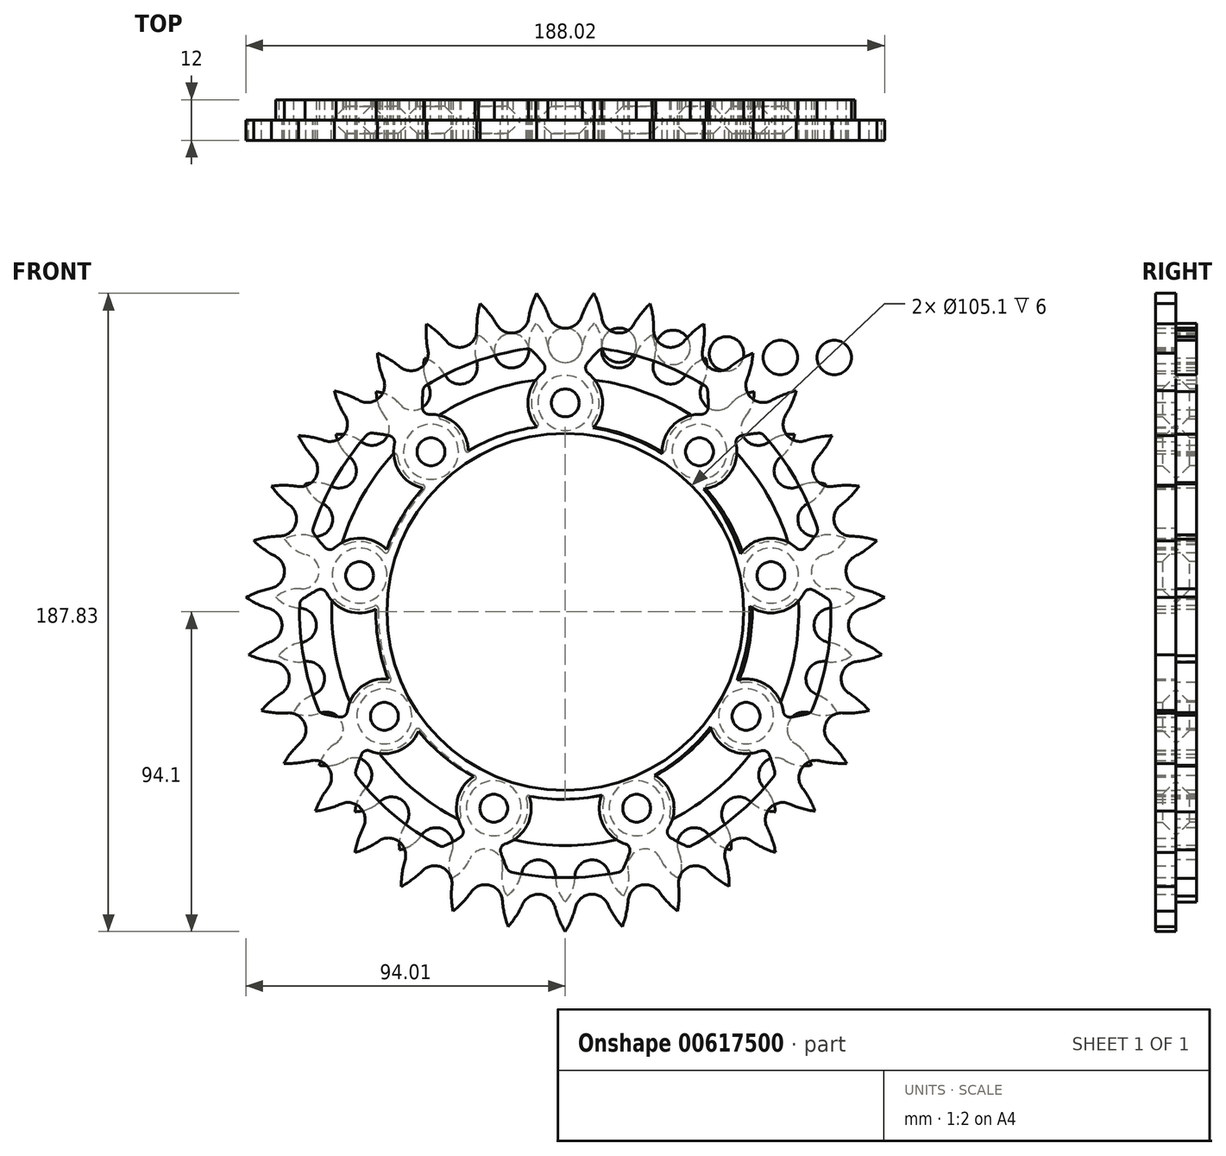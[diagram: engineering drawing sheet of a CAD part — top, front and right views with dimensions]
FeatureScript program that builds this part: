
annotation { "Feature Type Name" : "Feature", "Feature Type Description" : "" }
export const myFeature = defineFeature(function(context is Context, id is Id, definition is map)
    precondition{}
    {
        {
            var Q0;
            Q0=qCreatedBy(makeId("Front.planeOp"),FACE);
            var sketch = newSketch(context, id + "F0", { "sketchPlane" : qUnion([Q0])});
            skPoint(sketch, "E0.center", {"position": v(0, 0) * mm});
            skArc(sketch, "E1", {"start": v(-5.05, 77.94) * mm, "mid": v(0, 73.38) * mm, "end": v(5.05, 77.94) * mm});
            skArc(sketch, "E2", {"start": v(-5.05, 77.94) * mm, "mid": v(-6.19, 81.78) * mm, "end": v(-8.64, 84.93) * mm});
            skArc(sketch, "E3.trimOffspring", {"start": v(8.64, 84.93) * mm, "mid": v(6.19, 81.78) * mm, "end": v(5.05, 77.94) * mm});
            skArc(sketch, "E4.1.0", {"start": v(-20.64, 75.33) * mm, "mid": v(-22.52, 78.86) * mm, "end": v(-25.56, 81.46) * mm});
            skArc(sketch, "E4.1.1", {"start": v(-20.64, 75.33) * mm, "mid": v(-14.77, 71.88) * mm, "end": v(-10.74, 77.37) * mm});
            skArc(sketch, "E4.1.2", {"start": v(-8.64, 84.93) * mm, "mid": v(-10.4, 81.35) * mm, "end": v(-10.74, 77.37) * mm});
            skArc(sketch, "E4.2.0", {"start": v(-35.38, 69.63) * mm, "mid": v(-37.93, 72.7) * mm, "end": v(-41.43, 74.64) * mm});
            skArc(sketch, "E4.2.1", {"start": v(-35.38, 69.63) * mm, "mid": v(-28.94, 67.43) * mm, "end": v(-26.1, 73.62) * mm});
            skArc(sketch, "E4.2.2", {"start": v(-25.56, 81.46) * mm, "mid": v(-26.56, 77.59) * mm, "end": v(-26.1, 73.62) * mm});
            skArc(sketch, "E4.3.0", {"start": v(-48.68, 61.09) * mm, "mid": v(-51.8, 63.58) * mm, "end": v(-55.6, 64.78) * mm});
            skArc(sketch, "E4.3.1", {"start": v(-48.68, 61.09) * mm, "mid": v(-41.92, 60.23) * mm, "end": v(-40.38, 66.86) * mm});
            skArc(sketch, "E4.3.2", {"start": v(-41.43, 74.64) * mm, "mid": v(-41.64, 70.65) * mm, "end": v(-40.38, 66.86) * mm});
            skArc(sketch, "E4.4.0", {"start": v(-59.98, 50.04) * mm, "mid": v(-63.53, 51.86) * mm, "end": v(-67.51, 52.26) * mm});
            skArc(sketch, "E4.4.1", {"start": v(-59.98, 50.04) * mm, "mid": v(-53.18, 50.56) * mm, "end": v(-53.01, 57.36) * mm});
            skArc(sketch, "E4.4.2", {"start": v(-55.6, 64.78) * mm, "mid": v(-55, 60.83) * mm, "end": v(-53.01, 57.36) * mm});
            skArc(sketch, "E4.5.0", {"start": v(-68.82, 36.94) * mm, "mid": v(-72.67, 38) * mm, "end": v(-76.65, 37.6) * mm});
            skArc(sketch, "E4.5.1", {"start": v(-68.82, 36.94) * mm, "mid": v(-62.27, 38.81) * mm, "end": v(-63.47, 45.52) * mm});
            skArc(sketch, "E4.5.2", {"start": v(-67.51, 52.26) * mm, "mid": v(-66.13, 48.5) * mm, "end": v(-63.47, 45.52) * mm});
            skArc(sketch, "E4.6.0", {"start": v(-74.85, 22.33) * mm, "mid": v(-78.84, 22.6) * mm, "end": v(-82.65, 21.4) * mm});
            skArc(sketch, "E4.6.1", {"start": v(-74.85, 22.33) * mm, "mid": v(-68.81, 25.48) * mm, "end": v(-71.34, 31.8) * mm});
            skArc(sketch, "E4.6.2", {"start": v(-76.65, 37.6) * mm, "mid": v(-74.54, 34.2) * mm, "end": v(-71.34, 31.8) * mm});
            skArc(sketch, "E4.7.0", {"start": v(-77.81, 6.8) * mm, "mid": v(-81.77, 6.27) * mm, "end": v(-85.26, 4.32) * mm});
            skArc(sketch, "E4.7.1", {"start": v(-77.81, 6.8) * mm, "mid": v(-72.53, 11.11) * mm, "end": v(-76.28, 16.8) * mm});
            skArc(sketch, "E4.7.2", {"start": v(-82.65, 21.4) * mm, "mid": v(-79.9, 18.5) * mm, "end": v(-76.28, 16.8) * mm});
            skArc(sketch, "E4.8.0", {"start": v(-77.59, -9) * mm, "mid": v(-81.36, -10.32) * mm, "end": v(-84.39, -12.93) * mm});
            skArc(sketch, "E4.8.1", {"start": v(-77.59, -9) * mm, "mid": v(-73.28, -3.72) * mm, "end": v(-78.1, 1.1) * mm});
            skArc(sketch, "E4.8.2", {"start": v(-85.26, 4.32) * mm, "mid": v(-81.99, 2.04) * mm, "end": v(-78.1, 1.1) * mm});
            skArc(sketch, "E4.9.0", {"start": v(-74.19, -24.43) * mm, "mid": v(-77.62, -26.49) * mm, "end": v(-80.06, -29.65) * mm});
            skArc(sketch, "E4.9.1", {"start": v(-74.19, -24.43) * mm, "mid": v(-71.04, -18.4) * mm, "end": v(-76.72, -14.64) * mm});
            skArc(sketch, "E4.9.2", {"start": v(-84.39, -12.93) * mm, "mid": v(-80.72, -14.5) * mm, "end": v(-76.72, -14.64) * mm});
            skArc(sketch, "E4.10.0", {"start": v(-67.75, -38.86) * mm, "mid": v(-70.7, -41.57) * mm, "end": v(-72.45, -45.16) * mm});
            skArc(sketch, "E4.10.1", {"start": v(-67.75, -38.86) * mm, "mid": v(-65.88, -32.32) * mm, "end": v(-72.2, -29.79) * mm});
            skArc(sketch, "E4.10.2", {"start": v(-80.06, -29.65) * mm, "mid": v(-76.14, -30.46) * mm, "end": v(-72.2, -29.79) * mm});
            skArc(sketch, "E4.11.0", {"start": v(-58.54, -51.7) * mm, "mid": v(-60.88, -54.95) * mm, "end": v(-61.88, -58.82) * mm});
            skArc(sketch, "E4.11.1", {"start": v(-58.54, -51.7) * mm, "mid": v(-58.03, -44.92) * mm, "end": v(-64.73, -43.71) * mm});
            skArc(sketch, "E4.11.2", {"start": v(-72.45, -45.16) * mm, "mid": v(-68.45, -45.16) * mm, "end": v(-64.73, -43.71) * mm});
            skArc(sketch, "E4.12.0", {"start": v(-46.94, -62.43) * mm, "mid": v(-48.57, -66.08) * mm, "end": v(-48.77, -70.07) * mm});
            skArc(sketch, "E4.12.1", {"start": v(-46.94, -62.43) * mm, "mid": v(-47.8, -55.68) * mm, "end": v(-54.6, -55.85) * mm});
            skArc(sketch, "E4.12.2", {"start": v(-61.88, -58.82) * mm, "mid": v(-57.96, -58.02) * mm, "end": v(-54.6, -55.85) * mm});
            skArc(sketch, "E4.13.0", {"start": v(-33.4, -70.6) * mm, "mid": v(-34.28, -74.5) * mm, "end": v(-33.67, -78.45) * mm});
            skArc(sketch, "E4.13.1", {"start": v(-33.4, -70.6) * mm, "mid": v(-35.61, -64.16) * mm, "end": v(-42.25, -65.7) * mm});
            skArc(sketch, "E4.13.2", {"start": v(-48.77, -70.07) * mm, "mid": v(-45.1, -68.5) * mm, "end": v(-42.25, -65.7) * mm});
            skArc(sketch, "E4.14.0", {"start": v(-18.51, -75.88) * mm, "mid": v(-18.58, -79.88) * mm, "end": v(-17.19, -83.62) * mm});
            skArc(sketch, "E4.14.1", {"start": v(-18.51, -75.88) * mm, "mid": v(-21.97, -70.01) * mm, "end": v(-28.16, -72.86) * mm});
            skArc(sketch, "E4.14.2", {"start": v(-33.67, -78.45) * mm, "mid": v(-30.38, -76.17) * mm, "end": v(-28.16, -72.86) * mm});
            skArc(sketch, "E4.15.0", {"start": v(-2.86, -78.06) * mm, "mid": v(-2.12, -81.98) * mm, "end": v(0, -85.37) * mm});
            skArc(sketch, "E4.15.1", {"start": v(-2.86, -78.06) * mm, "mid": v(-7.42, -73) * mm, "end": v(-12.91, -77.03) * mm});
            skArc(sketch, "E4.15.2", {"start": v(-17.19, -83.62) * mm, "mid": v(-14.43, -80.73) * mm, "end": v(-12.91, -77.03) * mm});
            skArc(sketch, "E4.16.0", {"start": v(12.91, -77.03) * mm, "mid": v(14.43, -80.73) * mm, "end": v(17.19, -83.62) * mm});
            skArc(sketch, "E4.16.1", {"start": v(12.91, -77.03) * mm, "mid": v(7.42, -73) * mm, "end": v(2.86, -78.06) * mm});
            skArc(sketch, "E4.16.2", {"start": v(0, -85.37) * mm, "mid": v(2.12, -81.98) * mm, "end": v(2.86, -78.06) * mm});
            skArc(sketch, "E4.17.0", {"start": v(28.16, -72.86) * mm, "mid": v(30.38, -76.17) * mm, "end": v(33.67, -78.45) * mm});
            skArc(sketch, "E4.17.1", {"start": v(28.16, -72.86) * mm, "mid": v(21.97, -70.01) * mm, "end": v(18.51, -75.88) * mm});
            skArc(sketch, "E4.17.2", {"start": v(17.19, -83.62) * mm, "mid": v(18.58, -79.88) * mm, "end": v(18.51, -75.88) * mm});
            skArc(sketch, "E4.18.0", {"start": v(42.25, -65.7) * mm, "mid": v(45.1, -68.5) * mm, "end": v(48.77, -70.07) * mm});
            skArc(sketch, "E4.18.1", {"start": v(42.25, -65.7) * mm, "mid": v(35.61, -64.16) * mm, "end": v(33.4, -70.6) * mm});
            skArc(sketch, "E4.18.2", {"start": v(33.67, -78.45) * mm, "mid": v(34.28, -74.5) * mm, "end": v(33.4, -70.6) * mm});
            skArc(sketch, "E4.19.0", {"start": v(54.6, -55.85) * mm, "mid": v(57.96, -58.02) * mm, "end": v(61.88, -58.82) * mm});
            skArc(sketch, "E4.19.1", {"start": v(54.6, -55.85) * mm, "mid": v(47.8, -55.68) * mm, "end": v(46.94, -62.43) * mm});
            skArc(sketch, "E4.19.2", {"start": v(48.77, -70.07) * mm, "mid": v(48.57, -66.08) * mm, "end": v(46.94, -62.43) * mm});
            skArc(sketch, "E4.20.0", {"start": v(64.73, -43.71) * mm, "mid": v(68.45, -45.16) * mm, "end": v(72.45, -45.16) * mm});
            skArc(sketch, "E4.20.1", {"start": v(64.73, -43.71) * mm, "mid": v(58.03, -44.92) * mm, "end": v(58.54, -51.7) * mm});
            skArc(sketch, "E4.20.2", {"start": v(61.88, -58.82) * mm, "mid": v(60.88, -54.95) * mm, "end": v(58.54, -51.7) * mm});
            skArc(sketch, "E4.21.0", {"start": v(72.2, -29.79) * mm, "mid": v(76.14, -30.46) * mm, "end": v(80.06, -29.65) * mm});
            skArc(sketch, "E4.21.1", {"start": v(72.2, -29.79) * mm, "mid": v(65.88, -32.32) * mm, "end": v(67.75, -38.86) * mm});
            skArc(sketch, "E4.21.2", {"start": v(72.45, -45.16) * mm, "mid": v(70.7, -41.57) * mm, "end": v(67.75, -38.86) * mm});
            skArc(sketch, "E4.22.0", {"start": v(76.72, -14.64) * mm, "mid": v(80.72, -14.5) * mm, "end": v(84.39, -12.93) * mm});
            skArc(sketch, "E4.22.1", {"start": v(76.72, -14.64) * mm, "mid": v(71.04, -18.4) * mm, "end": v(74.19, -24.43) * mm});
            skArc(sketch, "E4.22.2", {"start": v(80.06, -29.65) * mm, "mid": v(77.62, -26.49) * mm, "end": v(74.19, -24.43) * mm});
            skArc(sketch, "E4.23.0", {"start": v(78.1, 1.1) * mm, "mid": v(81.99, 2.04) * mm, "end": v(85.26, 4.32) * mm});
            skArc(sketch, "E4.23.1", {"start": v(78.1, 1.1) * mm, "mid": v(73.28, -3.72) * mm, "end": v(77.59, -9) * mm});
            skArc(sketch, "E4.23.2", {"start": v(84.39, -12.93) * mm, "mid": v(81.36, -10.32) * mm, "end": v(77.59, -9) * mm});
            skArc(sketch, "E4.24.0", {"start": v(76.28, 16.8) * mm, "mid": v(79.9, 18.5) * mm, "end": v(82.65, 21.4) * mm});
            skArc(sketch, "E4.24.1", {"start": v(76.28, 16.8) * mm, "mid": v(72.53, 11.11) * mm, "end": v(77.81, 6.8) * mm});
            skArc(sketch, "E4.24.2", {"start": v(85.26, 4.32) * mm, "mid": v(81.77, 6.27) * mm, "end": v(77.81, 6.8) * mm});
            skArc(sketch, "E4.25.0", {"start": v(71.34, 31.8) * mm, "mid": v(74.54, 34.2) * mm, "end": v(76.65, 37.6) * mm});
            skArc(sketch, "E4.25.1", {"start": v(71.34, 31.8) * mm, "mid": v(68.81, 25.48) * mm, "end": v(74.85, 22.33) * mm});
            skArc(sketch, "E4.25.2", {"start": v(82.65, 21.4) * mm, "mid": v(78.84, 22.6) * mm, "end": v(74.85, 22.33) * mm});
            skArc(sketch, "E4.26.0", {"start": v(63.47, 45.52) * mm, "mid": v(66.13, 48.5) * mm, "end": v(67.51, 52.26) * mm});
            skArc(sketch, "E4.26.1", {"start": v(63.47, 45.52) * mm, "mid": v(62.27, 38.81) * mm, "end": v(68.82, 36.94) * mm});
            skArc(sketch, "E4.26.2", {"start": v(76.65, 37.6) * mm, "mid": v(72.67, 38) * mm, "end": v(68.82, 36.94) * mm});
            skArc(sketch, "E4.27.0", {"start": v(53.01, 57.36) * mm, "mid": v(55, 60.83) * mm, "end": v(55.6, 64.78) * mm});
            skArc(sketch, "E4.27.1", {"start": v(53.01, 57.36) * mm, "mid": v(53.18, 50.56) * mm, "end": v(59.98, 50.04) * mm});
            skArc(sketch, "E4.27.2", {"start": v(67.51, 52.26) * mm, "mid": v(63.53, 51.86) * mm, "end": v(59.98, 50.04) * mm});
            skArc(sketch, "E4.28.0", {"start": v(40.38, 66.86) * mm, "mid": v(41.64, 70.65) * mm, "end": v(41.43, 74.64) * mm});
            skArc(sketch, "E4.28.1", {"start": v(40.38, 66.86) * mm, "mid": v(41.92, 60.23) * mm, "end": v(48.68, 61.09) * mm});
            skArc(sketch, "E4.28.2", {"start": v(55.6, 64.78) * mm, "mid": v(51.8, 63.58) * mm, "end": v(48.68, 61.09) * mm});
            skArc(sketch, "E4.29.0", {"start": v(26.1, 73.62) * mm, "mid": v(26.56, 77.59) * mm, "end": v(25.56, 81.46) * mm});
            skArc(sketch, "E4.29.1", {"start": v(26.1, 73.62) * mm, "mid": v(28.94, 67.43) * mm, "end": v(35.38, 69.63) * mm});
            skArc(sketch, "E4.29.2", {"start": v(41.43, 74.64) * mm, "mid": v(37.93, 72.7) * mm, "end": v(35.38, 69.63) * mm});
            skArc(sketch, "E4.30.0", {"start": v(10.74, 77.37) * mm, "mid": v(10.4, 81.35) * mm, "end": v(8.64, 84.93) * mm});
            skArc(sketch, "E4.30.1", {"start": v(10.74, 77.37) * mm, "mid": v(14.77, 71.88) * mm, "end": v(20.64, 75.33) * mm});
            skArc(sketch, "E4.30.2", {"start": v(25.56, 81.46) * mm, "mid": v(22.52, 78.86) * mm, "end": v(20.64, 75.33) * mm});
            skCircle(sketch, "E5", {"center": v(-15.8, 76.85) * mm, "radius": 5.07 * mm});
            skCircle(sketch, "E6", {"center": v(0, 78.46) * mm, "radius": 5.07 * mm});
            skCircle(sketch, "E7", {"center": v(15.88, 78.46) * mm, "radius": 5.07 * mm});
            skCircle(sketch, "E8", {"center": v(31.74, 77.84) * mm, "radius": 5.07 * mm});
            skCircle(sketch, "E9", {"center": v(47.5, 75.94) * mm, "radius": 5.07 * mm});
            skCircle(sketch, "E10", {"center": v(63.34, 74.85) * mm, "radius": 5.07 * mm});
            skCircle(sketch, "E11", {"center": v(79.22, 74.85) * mm, "radius": 5.07 * mm});
            skCircle(sketch, "E12", {"center": v(0, 0) * mm, "radius": 52.55 * mm});
            skPoint(sketch, "E13", {"position": v(-39.53, 47.11) * mm});
            skPoint(sketch, "E14", {"position": v(0, 61.5) * mm});
            skPoint(sketch, "E15", {"position": v(39.53, 47.11) * mm});
            skPoint(sketch, "E16", {"position": v(60.57, 10.68) * mm});
            skPoint(sketch, "E17", {"position": v(53.26, -30.75) * mm});
            skPoint(sketch, "E18", {"position": v(21.03, -57.8) * mm});
            skPoint(sketch, "E19", {"position": v(-21.03, -57.8) * mm});
            skPoint(sketch, "E20", {"position": v(-53.26, -30.75) * mm});
            skPoint(sketch, "E21", {"position": v(-60.57, 10.68) * mm});
            skArc(sketch, "E22", {"start": v(11.44, -54.97) * mm, "mid": v(11.55, -60.96) * mm, "end": v(15.06, -65.81) * mm});
            skArc(sketch, "E23", {"start": v(-15.06, -65.81) * mm, "mid": v(-11.55, -60.96) * mm, "end": v(-11.44, -54.97) * mm});
            skArc(sketch, "E24", {"start": v(-10.58, -54.02) * mm, "mid": v(0, -55.05) * mm, "end": v(10.58, -54.02) * mm});
            skArc(sketch, "E25", {"start": v(-14.77, -67.14) * mm, "mid": v(0, -68.75) * mm, "end": v(14.77, -67.14) * mm});
            skPoint(sketch, "E26.visualSharp", {"position": v(-16.55, -66.73) * mm});
            skArc(sketch, "E26.filletArc", {"start": v(-15.06, -65.81) * mm, "mid": v(-15.34, -66.57) * mm, "end": v(-14.77, -67.14) * mm});
            skPoint(sketch, "E27.visualSharp", {"position": v(16.55, -66.73) * mm});
            skArc(sketch, "E27.filletArc", {"start": v(14.77, -67.14) * mm, "mid": v(15.34, -66.57) * mm, "end": v(15.06, -65.81) * mm});
            skPoint(sketch, "E28.visualSharp", {"position": v(11.89, -53.75) * mm});
            skArc(sketch, "E28.filletArc", {"start": v(11.44, -54.97) * mm, "mid": v(11.27, -54.26) * mm, "end": v(10.58, -54.02) * mm});
            skPoint(sketch, "E29.visualSharp", {"position": v(-11.89, -53.75) * mm});
            skArc(sketch, "E29.filletArc", {"start": v(-10.58, -54.02) * mm, "mid": v(-11.27, -54.26) * mm, "end": v(-11.44, -54.97) * mm});
            skArc(sketch, "E30.1.0", {"start": v(30.77, -60.1) * mm, "mid": v(30.34, -54.12) * mm, "end": v(26.57, -49.46) * mm});
            skArc(sketch, "E30.1.1", {"start": v(26.62, -48.18) * mm, "mid": v(26.24, -48.8) * mm, "end": v(26.57, -49.46) * mm});
            skArc(sketch, "E30.1.2", {"start": v(26.62, -48.18) * mm, "mid": v(35.39, -42.17) * mm, "end": v(42.83, -34.59) * mm});
            skArc(sketch, "E30.1.3", {"start": v(44.1, -34.76) * mm, "mid": v(43.51, -34.31) * mm, "end": v(42.83, -34.59) * mm});
            skArc(sketch, "E30.1.4", {"start": v(44.1, -34.76) * mm, "mid": v(48.03, -39.27) * mm, "end": v(53.84, -40.73) * mm});
            skArc(sketch, "E30.1.5", {"start": v(54.48, -41.94) * mm, "mid": v(54.54, -41.13) * mm, "end": v(53.84, -40.73) * mm});
            skArc(sketch, "E30.1.6", {"start": v(31.84, -60.93) * mm, "mid": v(44.2, -52.67) * mm, "end": v(54.48, -41.94) * mm});
            skArc(sketch, "E30.1.7", {"start": v(30.77, -60.1) * mm, "mid": v(31.04, -60.86) * mm, "end": v(31.84, -60.93) * mm});
            skArc(sketch, "E30.2.0", {"start": v(62.2, -26.26) * mm, "mid": v(58.03, -21.96) * mm, "end": v(52.15, -20.81) * mm});
            skArc(sketch, "E30.2.1", {"start": v(51.37, -19.8) * mm, "mid": v(51.47, -20.52) * mm, "end": v(52.15, -20.81) * mm});
            skArc(sketch, "E30.2.2", {"start": v(51.37, -19.8) * mm, "mid": v(54.21, -9.56) * mm, "end": v(55.04, 1.03) * mm});
            skArc(sketch, "E30.2.3", {"start": v(56.12, 1.72) * mm, "mid": v(55.39, 1.68) * mm, "end": v(55.04, 1.03) * mm});
            skArc(sketch, "E30.2.4", {"start": v(56.12, 1.72) * mm, "mid": v(62.04, 0.79) * mm, "end": v(67.43, 3.4) * mm});
            skArc(sketch, "E30.2.5", {"start": v(68.69, 2.89) * mm, "mid": v(68.22, 3.55) * mm, "end": v(67.43, 3.4) * mm});
            skArc(sketch, "E30.2.6", {"start": v(63.56, -26.2) * mm, "mid": v(67.7, -11.94) * mm, "end": v(68.69, 2.89) * mm});
            skArc(sketch, "E30.2.7", {"start": v(62.2, -26.26) * mm, "mid": v(62.9, -26.67) * mm, "end": v(63.56, -26.2) * mm});
            skArc(sketch, "E30.3.0", {"start": v(64.52, 19.86) * mm, "mid": v(58.57, 20.48) * mm, "end": v(53.33, 17.58) * mm});
            skArc(sketch, "E30.3.1", {"start": v(52.07, 17.85) * mm, "mid": v(52.62, 17.36) * mm, "end": v(53.33, 17.58) * mm});
            skArc(sketch, "E30.3.2", {"start": v(52.07, 17.85) * mm, "mid": v(47.67, 27.52) * mm, "end": v(41.5, 36.17) * mm});
            skArc(sketch, "E30.3.3", {"start": v(41.89, 37.4) * mm, "mid": v(41.35, 36.9) * mm, "end": v(41.5, 36.17) * mm});
            skArc(sketch, "E30.3.4", {"start": v(41.89, 37.4) * mm, "mid": v(47.02, 40.48) * mm, "end": v(49.46, 45.95) * mm});
            skArc(sketch, "E30.3.5", {"start": v(50.76, 46.37) * mm, "mid": v(49.98, 46.57) * mm, "end": v(49.46, 45.95) * mm});
            skArc(sketch, "E30.3.6", {"start": v(65.53, 20.78) * mm, "mid": v(59.54, 34.37) * mm, "end": v(50.76, 46.37) * mm});
            skArc(sketch, "E30.3.7", {"start": v(64.52, 19.86) * mm, "mid": v(65.32, 20) * mm, "end": v(65.53, 20.78) * mm});
            skArc(sketch, "E30.4.0", {"start": v(36.66, 56.7) * mm, "mid": v(31.7, 53.33) * mm, "end": v(29.55, 47.74) * mm});
            skArc(sketch, "E30.4.1", {"start": v(28.42, 47.15) * mm, "mid": v(29.15, 47.13) * mm, "end": v(29.55, 47.74) * mm});
            skArc(sketch, "E30.4.2", {"start": v(28.42, 47.15) * mm, "mid": v(18.83, 51.73) * mm, "end": v(8.54, 54.38) * mm});
            skArc(sketch, "E30.4.3", {"start": v(8.05, 55.57) * mm, "mid": v(7.96, 54.84) * mm, "end": v(8.54, 54.38) * mm});
            skArc(sketch, "E30.4.4", {"start": v(8.05, 55.57) * mm, "mid": v(10, 61.23) * mm, "end": v(8.36, 67) * mm});
            skArc(sketch, "E30.4.5", {"start": v(9.08, 68.15) * mm, "mid": v(8.35, 67.8) * mm, "end": v(8.36, 67) * mm});
            skArc(sketch, "E30.4.6", {"start": v(36.85, 58.04) * mm, "mid": v(23.51, 64.6) * mm, "end": v(9.08, 68.15) * mm});
            skArc(sketch, "E30.4.7", {"start": v(36.66, 56.7) * mm, "mid": v(37.19, 57.3) * mm, "end": v(36.85, 58.04) * mm});
            skArc(sketch, "E30.5.0", {"start": v(-8.36, 67) * mm, "mid": v(-10, 61.23) * mm, "end": v(-8.05, 55.57) * mm});
            skArc(sketch, "E30.5.1", {"start": v(-8.54, 54.38) * mm, "mid": v(-7.96, 54.84) * mm, "end": v(-8.05, 55.57) * mm});
            skArc(sketch, "E30.5.2", {"start": v(-8.54, 54.38) * mm, "mid": v(-18.83, 51.73) * mm, "end": v(-28.42, 47.15) * mm});
            skArc(sketch, "E30.5.3", {"start": v(-29.55, 47.74) * mm, "mid": v(-29.15, 47.13) * mm, "end": v(-28.42, 47.15) * mm});
            skArc(sketch, "E30.5.4", {"start": v(-29.55, 47.74) * mm, "mid": v(-31.7, 53.33) * mm, "end": v(-36.66, 56.7) * mm});
            skArc(sketch, "E30.5.5", {"start": v(-36.85, 58.04) * mm, "mid": v(-37.19, 57.3) * mm, "end": v(-36.66, 56.7) * mm});
            skArc(sketch, "E30.5.6", {"start": v(-9.08, 68.15) * mm, "mid": v(-23.51, 64.6) * mm, "end": v(-36.85, 58.04) * mm});
            skArc(sketch, "E30.5.7", {"start": v(-8.36, 67) * mm, "mid": v(-8.35, 67.8) * mm, "end": v(-9.08, 68.15) * mm});
            skArc(sketch, "E30.6.0", {"start": v(-49.46, 45.95) * mm, "mid": v(-47.02, 40.48) * mm, "end": v(-41.89, 37.4) * mm});
            skArc(sketch, "E30.6.1", {"start": v(-41.5, 36.17) * mm, "mid": v(-41.35, 36.9) * mm, "end": v(-41.89, 37.4) * mm});
            skArc(sketch, "E30.6.2", {"start": v(-41.5, 36.17) * mm, "mid": v(-47.67, 27.52) * mm, "end": v(-52.07, 17.85) * mm});
            skArc(sketch, "E30.6.3", {"start": v(-53.33, 17.58) * mm, "mid": v(-52.62, 17.36) * mm, "end": v(-52.07, 17.85) * mm});
            skArc(sketch, "E30.6.4", {"start": v(-53.33, 17.58) * mm, "mid": v(-58.57, 20.48) * mm, "end": v(-64.52, 19.86) * mm});
            skArc(sketch, "E30.6.5", {"start": v(-65.53, 20.78) * mm, "mid": v(-65.32, 20) * mm, "end": v(-64.52, 19.86) * mm});
            skArc(sketch, "E30.6.6", {"start": v(-50.76, 46.37) * mm, "mid": v(-59.54, 34.37) * mm, "end": v(-65.53, 20.78) * mm});
            skArc(sketch, "E30.6.7", {"start": v(-49.46, 45.95) * mm, "mid": v(-49.98, 46.57) * mm, "end": v(-50.76, 46.37) * mm});
            skArc(sketch, "E30.7.0", {"start": v(-67.43, 3.4) * mm, "mid": v(-62.04, 0.79) * mm, "end": v(-56.12, 1.72) * mm});
            skArc(sketch, "E30.7.1", {"start": v(-55.04, 1.03) * mm, "mid": v(-55.39, 1.68) * mm, "end": v(-56.12, 1.72) * mm});
            skArc(sketch, "E30.7.2", {"start": v(-55.04, 1.03) * mm, "mid": v(-54.21, -9.56) * mm, "end": v(-51.37, -19.8) * mm});
            skArc(sketch, "E30.7.3", {"start": v(-52.15, -20.81) * mm, "mid": v(-51.47, -20.52) * mm, "end": v(-51.37, -19.8) * mm});
            skArc(sketch, "E30.7.4", {"start": v(-52.15, -20.81) * mm, "mid": v(-58.03, -21.96) * mm, "end": v(-62.2, -26.26) * mm});
            skArc(sketch, "E30.7.5", {"start": v(-63.56, -26.2) * mm, "mid": v(-62.9, -26.67) * mm, "end": v(-62.2, -26.26) * mm});
            skArc(sketch, "E30.7.6", {"start": v(-68.69, 2.89) * mm, "mid": v(-67.7, -11.94) * mm, "end": v(-63.56, -26.2) * mm});
            skArc(sketch, "E30.7.7", {"start": v(-67.43, 3.4) * mm, "mid": v(-68.22, 3.55) * mm, "end": v(-68.69, 2.89) * mm});
            skArc(sketch, "E30.8.0", {"start": v(-53.84, -40.73) * mm, "mid": v(-48.03, -39.27) * mm, "end": v(-44.1, -34.76) * mm});
            skArc(sketch, "E30.8.1", {"start": v(-42.83, -34.59) * mm, "mid": v(-43.51, -34.31) * mm, "end": v(-44.1, -34.76) * mm});
            skArc(sketch, "E30.8.2", {"start": v(-42.83, -34.59) * mm, "mid": v(-35.39, -42.17) * mm, "end": v(-26.62, -48.18) * mm});
            skArc(sketch, "E30.8.3", {"start": v(-26.57, -49.46) * mm, "mid": v(-26.24, -48.8) * mm, "end": v(-26.62, -48.18) * mm});
            skArc(sketch, "E30.8.4", {"start": v(-26.57, -49.46) * mm, "mid": v(-30.34, -54.12) * mm, "end": v(-30.77, -60.1) * mm});
            skArc(sketch, "E30.8.5", {"start": v(-31.84, -60.93) * mm, "mid": v(-31.04, -60.86) * mm, "end": v(-30.77, -60.1) * mm});
            skArc(sketch, "E30.8.6", {"start": v(-54.48, -41.94) * mm, "mid": v(-44.2, -52.67) * mm, "end": v(-31.84, -60.93) * mm});
            skArc(sketch, "E30.8.7", {"start": v(-53.84, -40.73) * mm, "mid": v(-54.54, -41.13) * mm, "end": v(-54.48, -41.94) * mm});
            skSolve(sketch);
        }
        {
            var Q0;
            Q0 = qSketchRegion(id + "F0", true);
            extrude(context, id + "F1", {"entities" : qUnion([Q0]), "oppositeDirection" : true, "depth" : 6 * mm, "offsetDistance" : 25 * mm});
        }
        {
            var Q0;
            Q0=sQuery(id+"F0.wireOp",VERTEX,"E21");
            var Q1;
            Q1=sQuery(id+"F0.wireOp",VERTEX,"E13");
            var Q2;
            Q2=sQuery(id+"F0.wireOp",VERTEX,"E14");
            var Q3;
            Q3=sQuery(id+"F0.wireOp",VERTEX,"E15");
            var Q4;
            Q4=sQuery(id+"F0.wireOp",VERTEX,"E16");
            var Q5;
            Q5=sQuery(id+"F0.wireOp",VERTEX,"E17");
            var Q6;
            Q6=sQuery(id+"F0.wireOp",VERTEX,"E18");
            var Q7;
            Q7=sQuery(id+"F0.wireOp",VERTEX,"E19");
            var Q8;
            Q8=sQuery(id+"F0.wireOp",VERTEX,"E20");
            var Q9;
            Q9=makeQuery(id+"F1.opExtrude","SWEPT_BODY",BODY,{"disambiguationData":[OSD([sQuery(id+"F0.wireOp",EDGE,"E1"),sQuery(id+"F0.wireOp",EDGE,"E2"),sQuery(id+"F0.wireOp",EDGE,"E3.trimOffspring"),sQuery(id+"F0.wireOp",EDGE,"E4.1.0"),sQuery(id+"F0.wireOp",EDGE,"E4.1.1"),sQuery(id+"F0.wireOp",EDGE,"E4.1.2"),sQuery(id+"F0.wireOp",EDGE,"E4.2.0"),sQuery(id+"F0.wireOp",EDGE,"E4.2.1"),sQuery(id+"F0.wireOp",EDGE,"E4.2.2"),sQuery(id+"F0.wireOp",EDGE,"E4.3.0"),sQuery(id+"F0.wireOp",EDGE,"E4.3.1"),sQuery(id+"F0.wireOp",EDGE,"E4.3.2"),sQuery(id+"F0.wireOp",EDGE,"E4.4.0"),sQuery(id+"F0.wireOp",EDGE,"E4.4.1"),sQuery(id+"F0.wireOp",EDGE,"E4.4.2"),sQuery(id+"F0.wireOp",EDGE,"E4.5.0"),sQuery(id+"F0.wireOp",EDGE,"E4.5.1"),sQuery(id+"F0.wireOp",EDGE,"E4.5.2"),sQuery(id+"F0.wireOp",EDGE,"E4.6.0"),sQuery(id+"F0.wireOp",EDGE,"E4.6.1"),sQuery(id+"F0.wireOp",EDGE,"E4.6.2"),sQuery(id+"F0.wireOp",EDGE,"E4.7.0"),sQuery(id+"F0.wireOp",EDGE,"E4.7.1"),sQuery(id+"F0.wireOp",EDGE,"E4.7.2"),sQuery(id+"F0.wireOp",EDGE,"E4.8.0"),sQuery(id+"F0.wireOp",EDGE,"E4.8.1"),sQuery(id+"F0.wireOp",EDGE,"E4.8.2"),sQuery(id+"F0.wireOp",EDGE,"E4.9.0"),sQuery(id+"F0.wireOp",EDGE,"E4.9.1"),sQuery(id+"F0.wireOp",EDGE,"E4.9.2"),sQuery(id+"F0.wireOp",EDGE,"E4.10.0"),sQuery(id+"F0.wireOp",EDGE,"E4.10.1"),sQuery(id+"F0.wireOp",EDGE,"E4.10.2"),sQuery(id+"F0.wireOp",EDGE,"E4.11.0"),sQuery(id+"F0.wireOp",EDGE,"E4.11.1"),sQuery(id+"F0.wireOp",EDGE,"E4.11.2"),sQuery(id+"F0.wireOp",EDGE,"E4.12.0"),sQuery(id+"F0.wireOp",EDGE,"E4.12.1"),sQuery(id+"F0.wireOp",EDGE,"E4.12.2"),sQuery(id+"F0.wireOp",EDGE,"E4.13.0"),sQuery(id+"F0.wireOp",EDGE,"E4.13.1"),sQuery(id+"F0.wireOp",EDGE,"E4.13.2"),sQuery(id+"F0.wireOp",EDGE,"E4.14.0"),sQuery(id+"F0.wireOp",EDGE,"E4.14.1"),sQuery(id+"F0.wireOp",EDGE,"E4.14.2"),sQuery(id+"F0.wireOp",EDGE,"E4.15.0"),sQuery(id+"F0.wireOp",EDGE,"E4.15.1"),sQuery(id+"F0.wireOp",EDGE,"E4.15.2"),sQuery(id+"F0.wireOp",EDGE,"E4.16.0"),sQuery(id+"F0.wireOp",EDGE,"E4.16.1"),sQuery(id+"F0.wireOp",EDGE,"E4.16.2"),sQuery(id+"F0.wireOp",EDGE,"E4.17.0"),sQuery(id+"F0.wireOp",EDGE,"E4.17.1"),sQuery(id+"F0.wireOp",EDGE,"E4.17.2"),sQuery(id+"F0.wireOp",EDGE,"E4.18.0"),sQuery(id+"F0.wireOp",EDGE,"E4.18.1"),sQuery(id+"F0.wireOp",EDGE,"E4.18.2"),sQuery(id+"F0.wireOp",EDGE,"E4.19.0"),sQuery(id+"F0.wireOp",EDGE,"E4.19.1"),sQuery(id+"F0.wireOp",EDGE,"E4.19.2"),sQuery(id+"F0.wireOp",EDGE,"E4.20.0"),sQuery(id+"F0.wireOp",EDGE,"E4.20.1"),sQuery(id+"F0.wireOp",EDGE,"E4.20.2"),sQuery(id+"F0.wireOp",EDGE,"E4.21.0"),sQuery(id+"F0.wireOp",EDGE,"E4.21.1"),sQuery(id+"F0.wireOp",EDGE,"E4.21.2"),sQuery(id+"F0.wireOp",EDGE,"E4.22.0"),sQuery(id+"F0.wireOp",EDGE,"E4.22.1"),sQuery(id+"F0.wireOp",EDGE,"E4.22.2"),sQuery(id+"F0.wireOp",EDGE,"E4.23.0"),sQuery(id+"F0.wireOp",EDGE,"E4.23.1"),sQuery(id+"F0.wireOp",EDGE,"E4.23.2"),sQuery(id+"F0.wireOp",EDGE,"E4.24.0"),sQuery(id+"F0.wireOp",EDGE,"E4.24.1"),sQuery(id+"F0.wireOp",EDGE,"E4.24.2"),sQuery(id+"F0.wireOp",EDGE,"E4.25.0"),sQuery(id+"F0.wireOp",EDGE,"E4.25.1"),sQuery(id+"F0.wireOp",EDGE,"E4.25.2"),sQuery(id+"F0.wireOp",EDGE,"E4.26.0"),sQuery(id+"F0.wireOp",EDGE,"E4.26.1"),sQuery(id+"F0.wireOp",EDGE,"E4.26.2"),sQuery(id+"F0.wireOp",EDGE,"E4.27.0"),sQuery(id+"F0.wireOp",EDGE,"E4.27.1"),sQuery(id+"F0.wireOp",EDGE,"E4.27.2"),sQuery(id+"F0.wireOp",EDGE,"E4.28.0"),sQuery(id+"F0.wireOp",EDGE,"E4.28.1"),sQuery(id+"F0.wireOp",EDGE,"E4.28.2"),sQuery(id+"F0.wireOp",EDGE,"E4.29.0"),sQuery(id+"F0.wireOp",EDGE,"E4.29.1"),sQuery(id+"F0.wireOp",EDGE,"E4.29.2"),sQuery(id+"F0.wireOp",EDGE,"E4.30.0"),sQuery(id+"F0.wireOp",EDGE,"E4.30.1"),sQuery(id+"F0.wireOp",EDGE,"E4.30.2"),sQuery(id+"F0.wireOp",EDGE,"E12")])]});
            hole(context, id + "F2", {"style" : HoleStyle.C_SINK, "endStyle" : HoleEndStyle.THROUGH, "holeDiameter" : 8.2 * mm, "cSinkDiameter" : 16.2 * mm, "cSinkAngle" : 90 * degree, "majorDiameter" : 5 * mm, "isTappedThrough" : true, "tappedDepth" : 12 * mm, "tapClearance" : 3, "startFromSketch" : true, "locations" : qUnion([Q0, Q1, Q2, Q3, Q4, Q5, Q6, Q7, Q8]), "scope" : qUnion([Q9])});
        }
        {
            var Q0;
            Q0=qCreatedBy(makeId("Front.planeOp"),FACE);
            var sketch = newSketch(context, id + "F3", { "sketchPlane" : qUnion([Q0])});
            skPoint(sketch, "E31", {"position": v(0, 61.5) * mm});
            skPoint(sketch, "E32.3.0", {"position": v(-53.26, -30.75) * mm});
            skPoint(sketch, "E32.4.0", {"position": v(-21.03, -57.8) * mm});
            skPoint(sketch, "E32.5.0", {"position": v(21.03, -57.8) * mm});
            skPoint(sketch, "E32.6.0", {"position": v(53.26, -30.75) * mm});
            skPoint(sketch, "E32.7.0", {"position": v(60.57, 10.68) * mm});
            skPoint(sketch, "E32.8.0", {"position": v(39.53, 47.11) * mm});
            skPoint(sketch, "E32.center", {"position": v(0, 0) * mm});
            skArc(sketch, "E33", {"start": v(-4.8, 86.86) * mm, "mid": v(0, 83.47) * mm, "end": v(4.8, 86.86) * mm});
            skPoint(sketch, "E34.center", {"position": v(0, -0.73) * mm});
            skPoint(sketch, "E35", {"position": v(-60.57, 10.68) * mm});
            skPoint(sketch, "E36", {"position": v(-39.53, 47.11) * mm});
            skArc(sketch, "E37", {"start": v(10.72, -53.96) * mm, "mid": v(11.14, -62.6) * mm, "end": v(17.68, -68.27) * mm});
            skArc(sketch, "E38", {"start": v(-17.68, -68.27) * mm, "mid": v(-11.21, -62.75) * mm, "end": v(-10.61, -54.27) * mm});
            skArc(sketch, "E39", {"start": v(-15.72, -76.62) * mm, "mid": v(0, -78.23) * mm, "end": v(15.72, -76.62) * mm});
            skArc(sketch, "E40", {"start": v(17.12, -75.5) * mm, "mid": v(18.12, -73.17) * mm, "end": v(18.98, -70.8) * mm});
            skArc(sketch, "E41", {"start": v(-18.98, -70.8) * mm, "mid": v(-18.12, -73.17) * mm, "end": v(-17.12, -75.5) * mm});
            skPoint(sketch, "E42.visualSharp", {"position": v(-19.6, -68.7) * mm});
            skArc(sketch, "E42.filletArc", {"start": v(-17.68, -68.27) * mm, "mid": v(-18.85, -69.26) * mm, "end": v(-18.98, -70.8) * mm});
            skPoint(sketch, "E43.visualSharp", {"position": v(19.6, -68.7) * mm});
            skArc(sketch, "E43.filletArc", {"start": v(18.98, -70.8) * mm, "mid": v(18.85, -69.26) * mm, "end": v(17.68, -68.27) * mm});
            skPoint(sketch, "E44.visualSharp", {"position": v(16.69, -76.41) * mm});
            skArc(sketch, "E44.filletArc", {"start": v(15.72, -76.62) * mm, "mid": v(16.55, -76.23) * mm, "end": v(17.12, -75.5) * mm});
            skPoint(sketch, "E45.visualSharp", {"position": v(-16.69, -76.41) * mm});
            skArc(sketch, "E45.filletArc", {"start": v(-17.12, -75.5) * mm, "mid": v(-16.55, -76.23) * mm, "end": v(-15.72, -76.62) * mm});
            skArc(sketch, "E46.1.0", {"start": v(42.73, -33.91) * mm, "mid": v(48.53, -40.68) * mm, "end": v(57.44, -40.93) * mm});
            skArc(sketch, "E46.1.1", {"start": v(30.34, -63.67) * mm, "mid": v(31.68, -55) * mm, "end": v(26.25, -48.1) * mm});
            skArc(sketch, "E46.1.2", {"start": v(30.34, -63.67) * mm, "mid": v(30.09, -65.18) * mm, "end": v(30.98, -66.43) * mm});
            skArc(sketch, "E46.1.3", {"start": v(30.98, -66.43) * mm, "mid": v(33.16, -67.7) * mm, "end": v(35.42, -68.85) * mm});
            skArc(sketch, "E46.1.4", {"start": v(35.42, -68.85) * mm, "mid": v(36.33, -69.04) * mm, "end": v(37.22, -68.8) * mm});
            skArc(sketch, "E46.1.5", {"start": v(37.22, -68.8) * mm, "mid": v(50.3, -59.93) * mm, "end": v(61.3, -48.6) * mm});
            skArc(sketch, "E46.1.6", {"start": v(61.3, -48.6) * mm, "mid": v(61.69, -47.76) * mm, "end": v(61.66, -46.83) * mm});
            skArc(sketch, "E46.1.7", {"start": v(61.66, -46.83) * mm, "mid": v(60.92, -44.41) * mm, "end": v(60.05, -42.03) * mm});
            skArc(sketch, "E46.1.8", {"start": v(60.05, -42.03) * mm, "mid": v(58.97, -40.94) * mm, "end": v(57.44, -40.93) * mm});
            skArc(sketch, "E46.2.0", {"start": v(54.3, 1.65) * mm, "mid": v(63.2, 0) * mm, "end": v(70.32, 5.56) * mm});
            skArc(sketch, "E46.2.1", {"start": v(64.18, -29.27) * mm, "mid": v(59.43, -21.63) * mm, "end": v(50.58, -20.09) * mm});
            skArc(sketch, "E46.2.2", {"start": v(64.18, -29.27) * mm, "mid": v(64.95, -30.6) * mm, "end": v(66.44, -30.98) * mm});
            skArc(sketch, "E46.2.3", {"start": v(66.44, -30.98) * mm, "mid": v(68.93, -30.55) * mm, "end": v(71.4, -29.98) * mm});
            skArc(sketch, "E46.2.4", {"start": v(71.4, -29.98) * mm, "mid": v(72.21, -29.54) * mm, "end": v(72.74, -28.78) * mm});
            skArc(sketch, "E46.2.5", {"start": v(72.74, -28.78) * mm, "mid": v(77.06, -13.58) * mm, "end": v(78.2, 2.17) * mm});
            skArc(sketch, "E46.2.6", {"start": v(78.2, 2.17) * mm, "mid": v(77.96, 3.06) * mm, "end": v(77.34, 3.75) * mm});
            skArc(sketch, "E46.2.7", {"start": v(77.34, 3.75) * mm, "mid": v(75.23, 5.14) * mm, "end": v(73.03, 6.4) * mm});
            skArc(sketch, "E46.2.8", {"start": v(73.03, 6.4) * mm, "mid": v(71.5, 6.54) * mm, "end": v(70.32, 5.56) * mm});
            skArc(sketch, "E46.3.0", {"start": v(40.68, 36.18) * mm, "mid": v(48.46, 40.66) * mm, "end": v(50.3, 49.45) * mm});
            skArc(sketch, "E46.3.1", {"start": v(67.98, 18.83) * mm, "mid": v(59.38, 21.62) * mm, "end": v(51.6, 17.02) * mm});
            skArc(sketch, "E46.3.2", {"start": v(67.98, 18.83) * mm, "mid": v(69.43, 18.3) * mm, "end": v(70.81, 18.97) * mm});
            skArc(sketch, "E46.3.3", {"start": v(70.81, 18.97) * mm, "mid": v(72.45, 20.9) * mm, "end": v(73.97, 22.93) * mm});
            skArc(sketch, "E46.3.4", {"start": v(73.97, 22.93) * mm, "mid": v(74.31, 23.79) * mm, "end": v(74.23, 24.7) * mm});
            skArc(sketch, "E46.3.5", {"start": v(74.23, 24.7) * mm, "mid": v(67.77, 39.12) * mm, "end": v(58.52, 51.93) * mm});
            skArc(sketch, "E46.3.6", {"start": v(58.52, 51.93) * mm, "mid": v(57.76, 52.46) * mm, "end": v(56.85, 52.59) * mm});
            skArc(sketch, "E46.3.7", {"start": v(56.85, 52.59) * mm, "mid": v(54.33, 52.29) * mm, "end": v(51.84, 51.84) * mm});
            skArc(sketch, "E46.3.8", {"start": v(51.84, 51.84) * mm, "mid": v(50.57, 50.96) * mm, "end": v(50.3, 49.45) * mm});
            skArc(sketch, "E46.4.0", {"start": v(8.24, 54.2) * mm, "mid": v(10.97, 62.53) * mm, "end": v(6.75, 70.21) * mm});
            skArc(sketch, "E46.4.1", {"start": v(39.98, 58.12) * mm, "mid": v(31.7, 54.84) * mm, "end": v(28.57, 46.5) * mm});
            skArc(sketch, "E46.4.2", {"start": v(39.98, 58.12) * mm, "mid": v(41.42, 58.65) * mm, "end": v(42.06, 60.05) * mm});
            skArc(sketch, "E46.4.3", {"start": v(42.06, 60.05) * mm, "mid": v(42.07, 62.58) * mm, "end": v(41.93, 65.1) * mm});
            skArc(sketch, "E46.4.4", {"start": v(41.93, 65.1) * mm, "mid": v(41.64, 65.98) * mm, "end": v(41, 66.64) * mm});
            skArc(sketch, "E46.4.5", {"start": v(41, 66.64) * mm, "mid": v(26.77, 73.53) * mm, "end": v(11.46, 77.39) * mm});
            skArc(sketch, "E46.4.6", {"start": v(11.46, 77.39) * mm, "mid": v(10.54, 77.3) * mm, "end": v(9.75, 76.82) * mm});
            skArc(sketch, "E46.4.7", {"start": v(9.75, 76.82) * mm, "mid": v(8.02, 74.97) * mm, "end": v(6.4, 73.03) * mm});
            skArc(sketch, "E46.4.8", {"start": v(6.4, 73.03) * mm, "mid": v(6, 71.55) * mm, "end": v(6.75, 70.21) * mm});
            skArc(sketch, "E46.5.0", {"start": v(-28.52, 47.4) * mm, "mid": v(-32, 55.15) * mm, "end": v(-39.95, 58.12) * mm});
            skArc(sketch, "E46.5.1", {"start": v(-6.72, 70.22) * mm, "mid": v(-10.93, 62.66) * mm, "end": v(-8.38, 54.4) * mm});
            skArc(sketch, "E46.5.2", {"start": v(-6.72, 70.22) * mm, "mid": v(-5.96, 71.55) * mm, "end": v(-6.37, 73.03) * mm});
            skArc(sketch, "E46.5.3", {"start": v(-6.37, 73.03) * mm, "mid": v(-7.99, 74.98) * mm, "end": v(-9.72, 76.83) * mm});
            skArc(sketch, "E46.5.4", {"start": v(-9.72, 76.83) * mm, "mid": v(-10.5, 77.31) * mm, "end": v(-11.43, 77.4) * mm});
            skArc(sketch, "E46.5.5", {"start": v(-11.43, 77.4) * mm, "mid": v(-26.74, 73.53) * mm, "end": v(-40.96, 66.64) * mm});
            skArc(sketch, "E46.5.6", {"start": v(-40.96, 66.64) * mm, "mid": v(-41.61, 66) * mm, "end": v(-41.9, 65.11) * mm});
            skArc(sketch, "E46.5.7", {"start": v(-41.9, 65.11) * mm, "mid": v(-42.04, 62.58) * mm, "end": v(-42.03, 60.05) * mm});
            skArc(sketch, "E46.5.8", {"start": v(-42.03, 60.05) * mm, "mid": v(-41.4, 58.66) * mm, "end": v(-39.95, 58.12) * mm});
            skArc(sketch, "E46.6.0", {"start": v(-52.6, 18.3) * mm, "mid": v(-60.17, 21.7) * mm, "end": v(-67.96, 18.84) * mm});
            skArc(sketch, "E46.6.1", {"start": v(-50.28, 49.47) * mm, "mid": v(-48.8, 41.2) * mm, "end": v(-41.92, 36.4) * mm});
            skArc(sketch, "E46.6.2", {"start": v(-50.28, 49.47) * mm, "mid": v(-50.55, 50.98) * mm, "end": v(-51.81, 51.85) * mm});
            skArc(sketch, "E46.6.3", {"start": v(-51.81, 51.85) * mm, "mid": v(-54.3, 52.3) * mm, "end": v(-56.82, 52.6) * mm});
            skArc(sketch, "E46.6.4", {"start": v(-56.82, 52.6) * mm, "mid": v(-57.74, 52.47) * mm, "end": v(-58.5, 51.94) * mm});
            skArc(sketch, "E46.6.5", {"start": v(-58.5, 51.94) * mm, "mid": v(-67.74, 39.13) * mm, "end": v(-74.2, 24.72) * mm});
            skArc(sketch, "E46.6.6", {"start": v(-74.2, 24.72) * mm, "mid": v(-74.29, 23.8) * mm, "end": v(-73.95, 22.94) * mm});
            skArc(sketch, "E46.6.7", {"start": v(-73.95, 22.94) * mm, "mid": v(-72.43, 20.91) * mm, "end": v(-70.8, 18.98) * mm});
            skArc(sketch, "E46.6.8", {"start": v(-70.8, 18.98) * mm, "mid": v(-69.4, 18.32) * mm, "end": v(-67.96, 18.84) * mm});
            skArc(sketch, "E46.7.0", {"start": v(-52.13, -19.8) * mm, "mid": v(-60.06, -22.09) * mm, "end": v(-64.16, -29.25) * mm});
            skArc(sketch, "E46.7.1", {"start": v(-70.3, 5.57) * mm, "mid": v(-64, 0.24) * mm, "end": v(-55.76, 0.8) * mm});
            skArc(sketch, "E46.7.2", {"start": v(-70.3, 5.57) * mm, "mid": v(-71.48, 6.55) * mm, "end": v(-73.01, 6.4) * mm});
            skArc(sketch, "E46.7.3", {"start": v(-73.01, 6.4) * mm, "mid": v(-75.21, 5.15) * mm, "end": v(-77.33, 3.77) * mm});
            skArc(sketch, "E46.7.4", {"start": v(-77.33, 3.77) * mm, "mid": v(-77.95, 3.08) * mm, "end": v(-78.19, 2.19) * mm});
            skArc(sketch, "E46.7.5", {"start": v(-78.19, 2.19) * mm, "mid": v(-77.04, -13.57) * mm, "end": v(-72.73, -28.77) * mm});
            skArc(sketch, "E46.7.6", {"start": v(-72.73, -28.77) * mm, "mid": v(-72.2, -29.52) * mm, "end": v(-71.38, -29.96) * mm});
            skArc(sketch, "E46.7.7", {"start": v(-71.38, -29.96) * mm, "mid": v(-68.92, -30.54) * mm, "end": v(-66.42, -30.96) * mm});
            skArc(sketch, "E46.7.8", {"start": v(-66.42, -30.96) * mm, "mid": v(-64.94, -30.58) * mm, "end": v(-64.16, -29.25) * mm});
            skArc(sketch, "E46.8.0", {"start": v(-26.95, -48.5) * mm, "mid": v(-31.77, -55.38) * mm, "end": v(-30.34, -63.66) * mm});
            skArc(sketch, "E46.8.1", {"start": v(-57.43, -40.92) * mm, "mid": v(-49.13, -40.94) * mm, "end": v(-43.18, -35.15) * mm});
            skArc(sketch, "E46.8.2", {"start": v(-57.43, -40.92) * mm, "mid": v(-58.97, -40.93) * mm, "end": v(-60.04, -42.02) * mm});
            skArc(sketch, "E46.8.3", {"start": v(-60.04, -42.02) * mm, "mid": v(-60.92, -44.4) * mm, "end": v(-61.65, -46.82) * mm});
            skArc(sketch, "E46.8.4", {"start": v(-61.65, -46.82) * mm, "mid": v(-61.68, -47.75) * mm, "end": v(-61.3, -48.59) * mm});
            skArc(sketch, "E46.8.5", {"start": v(-61.3, -48.59) * mm, "mid": v(-50.29, -59.92) * mm, "end": v(-37.22, -68.79) * mm});
            skArc(sketch, "E46.8.6", {"start": v(-37.22, -68.79) * mm, "mid": v(-36.32, -69.03) * mm, "end": v(-35.42, -68.84) * mm});
            skArc(sketch, "E46.8.7", {"start": v(-35.42, -68.84) * mm, "mid": v(-33.16, -67.7) * mm, "end": v(-30.97, -66.42) * mm});
            skArc(sketch, "E46.8.8", {"start": v(-30.97, -66.42) * mm, "mid": v(-30.08, -65.17) * mm, "end": v(-30.34, -63.66) * mm});
            skCircle(sketch, "E47.converted", {"center": v(0, 0) * mm, "radius": 52.55 * mm});
            skArc(sketch, "E48", {"start": v(26.25, -48.1) * mm, "mid": v(35.2, -41.83) * mm, "end": v(42.73, -33.91) * mm});
            skPoint(sketch, "E49.orphan", {"position": v(12.31, -51.09) * mm});
            skPoint(sketch, "E50.orphan", {"position": v(23.41, -47.05) * mm});
            skPoint(sketch, "E51.orphan", {"position": v(-12.31, -51.09) * mm});
            skArc(sketch, "E52.trimOffspring", {"start": v(-10.61, -54.27) * mm, "mid": v(0.07, -55.16) * mm, "end": v(10.72, -53.96) * mm});
            skPoint(sketch, "E53.orphan", {"position": v(-23.4, -47.04) * mm});
            skPoint(sketch, "E54.orphan", {"position": v(-42.27, -31.21) * mm});
            skArc(sketch, "E55.trimOffspring", {"start": v(-43.18, -35.15) * mm, "mid": v(-35.71, -42.6) * mm, "end": v(-26.95, -48.5) * mm});
            skPoint(sketch, "E56.orphan", {"position": v(-48.17, -20.98) * mm});
            skArc(sketch, "E57.trimOffspring", {"start": v(-55.76, 0.8) * mm, "mid": v(-54.93, -9.67) * mm, "end": v(-52.13, -19.8) * mm});
            skPoint(sketch, "E58.orphan", {"position": v(-52.45, 3.27) * mm});
            skPoint(sketch, "E59.orphan", {"position": v(-50.4, 14.9) * mm});
            skPoint(sketch, "E60.orphan", {"position": v(-38.08, 36.23) * mm});
            skArc(sketch, "E61.trimOffspring", {"start": v(-41.92, 36.4) * mm, "mid": v(-48.14, 27.86) * mm, "end": v(-52.6, 18.3) * mm});
            skPoint(sketch, "E62.orphan", {"position": v(-29.03, 43.81) * mm});
            skPoint(sketch, "E63.orphan", {"position": v(-5.89, 52.24) * mm});
            skArc(sketch, "E64.trimOffspring", {"start": v(-8.38, 54.4) * mm, "mid": v(-18.8, 51.89) * mm, "end": v(-28.52, 47.4) * mm});
            skPoint(sketch, "E65.orphan", {"position": v(5.92, 52.23) * mm});
            skPoint(sketch, "E66.orphan", {"position": v(29.06, 43.8) * mm});
            skArc(sketch, "E67.trimOffspring", {"start": v(28.57, 46.5) * mm, "mid": v(18.79, 51.37) * mm, "end": v(8.24, 54.2) * mm});
            skPoint(sketch, "E68.orphan", {"position": v(38.1, 36.21) * mm});
            skPoint(sketch, "E69.orphan", {"position": v(50.42, 14.89) * mm});
            skArc(sketch, "E70.trimOffspring", {"start": v(51.6, 17.02) * mm, "mid": v(47.1, 27.15) * mm, "end": v(40.68, 36.18) * mm});
            skPoint(sketch, "E71.orphan", {"position": v(52.46, 3.25) * mm});
            skPoint(sketch, "E72.orphan", {"position": v(48.19, -21) * mm});
            skArc(sketch, "E73.trimOffspring", {"start": v(50.58, -20.09) * mm, "mid": v(53.54, -9.4) * mm, "end": v(54.3, 1.65) * mm});
            skPoint(sketch, "E74.orphan", {"position": v(42.28, -31.22) * mm});
            skArc(sketch, "E75", {"start": v(4.8, 86.86) * mm, "mid": v(6.36, 90.43) * mm, "end": v(8.44, 93.73) * mm});
            skArc(sketch, "E76", {"start": v(-4.8, 86.86) * mm, "mid": v(-6.36, 90.43) * mm, "end": v(-8.44, 93.73) * mm});
            skPoint(sketch, "E77.visualSharp", {"position": v(-8.51, 93.83) * mm});
            skPoint(sketch, "E78.visualSharp", {"position": v(8.51, 93.83) * mm});
            skArc(sketch, "E79.1.0", {"start": v(-20.22, 84.6) * mm, "mid": v(-22.44, 87.89) * mm, "end": v(-25.13, 90.8) * mm});
            skArc(sketch, "E79.1.1", {"start": v(-20.22, 84.6) * mm, "mid": v(-14.9, 82.13) * mm, "end": v(-10.8, 86.32) * mm});
            skArc(sketch, "E79.1.2", {"start": v(-10.8, 86.32) * mm, "mid": v(-9.9, 90.11) * mm, "end": v(-8.44, 93.73) * mm});
            skArc(sketch, "E79.2.0", {"start": v(-35, 79.64) * mm, "mid": v(-37.77, 82.47) * mm, "end": v(-40.94, 84.85) * mm});
            skArc(sketch, "E79.2.1", {"start": v(-35, 79.64) * mm, "mid": v(-29.33, 78.15) * mm, "end": v(-26.04, 83) * mm});
            skArc(sketch, "E79.2.2", {"start": v(-26.04, 83) * mm, "mid": v(-25.81, 86.96) * mm, "end": v(-25, 90.84) * mm});
            skArc(sketch, "E79.3.0", {"start": v(-48.66, 72.1) * mm, "mid": v(-51.9, 74.4) * mm, "end": v(-55.43, 76.18) * mm});
            skArc(sketch, "E79.3.1", {"start": v(-48.66, 72.1) * mm, "mid": v(-42.81, 71.65) * mm, "end": v(-40.44, 77.02) * mm});
            skArc(sketch, "E79.3.2", {"start": v(-40.44, 77.02) * mm, "mid": v(-40.93, 80.95) * mm, "end": v(-40.82, 84.91) * mm});
            skArc(sketch, "E79.4.0", {"start": v(-60.75, 62.26) * mm, "mid": v(-64.34, 63.94) * mm, "end": v(-68.14, 65.06) * mm});
            skArc(sketch, "E79.4.1", {"start": v(-60.75, 62.26) * mm, "mid": v(-54.92, 62.86) * mm, "end": v(-53.54, 68.56) * mm});
            skArc(sketch, "E79.4.2", {"start": v(-53.54, 68.56) * mm, "mid": v(-54.72, 72.34) * mm, "end": v(-55.32, 76.26) * mm});
            skArc(sketch, "E79.5.0", {"start": v(-70.9, 50.41) * mm, "mid": v(-74.73, 51.42) * mm, "end": v(-78.66, 51.85) * mm});
            skArc(sketch, "E79.5.1", {"start": v(-70.9, 50.41) * mm, "mid": v(-65.26, 52.04) * mm, "end": v(-64.92, 57.9) * mm});
            skArc(sketch, "E79.5.2", {"start": v(-64.92, 57.9) * mm, "mid": v(-66.76, 61.4) * mm, "end": v(-68.05, 65.15) * mm});
            skArc(sketch, "E79.6.0", {"start": v(-78.76, 36.94) * mm, "mid": v(-82.7, 37.25) * mm, "end": v(-86.66, 36.97) * mm});
            skArc(sketch, "E79.6.1", {"start": v(-78.76, 36.94) * mm, "mid": v(-73.5, 39.55) * mm, "end": v(-74.22, 45.38) * mm});
            skArc(sketch, "E79.6.2", {"start": v(-74.22, 45.38) * mm, "mid": v(-76.65, 48.5) * mm, "end": v(-78.6, 51.96) * mm});
            skArc(sketch, "E79.7.0", {"start": v(-84.09, 22.29) * mm, "mid": v(-88.03, 21.89) * mm, "end": v(-91.87, 20.9) * mm});
            skArc(sketch, "E79.7.1", {"start": v(-84.09, 22.29) * mm, "mid": v(-79.38, 25.8) * mm, "end": v(-81.13, 31.4) * mm});
            skArc(sketch, "E79.7.2", {"start": v(-81.13, 31.4) * mm, "mid": v(-84.08, 34.04) * mm, "end": v(-86.6, 37.09) * mm});
            skArc(sketch, "E79.8.0", {"start": v(-86.72, 6.91) * mm, "mid": v(-90.52, 5.82) * mm, "end": v(-94.12, 4.16) * mm});
            skArc(sketch, "E79.8.1", {"start": v(-86.72, 6.91) * mm, "mid": v(-82.71, 11.2) * mm, "end": v(-85.43, 16.4) * mm});
            skArc(sketch, "E79.8.2", {"start": v(-85.43, 16.4) * mm, "mid": v(-88.8, 18.48) * mm, "end": v(-91.84, 21.03) * mm});
            skArc(sketch, "E79.9.0", {"start": v(-86.56, -8.68) * mm, "mid": v(-90.1, -10.44) * mm, "end": v(-93.35, -12.71) * mm});
            skArc(sketch, "E79.9.1", {"start": v(-86.56, -8.68) * mm, "mid": v(-83.39, -3.74) * mm, "end": v(-86.99, 0.89) * mm});
            skArc(sketch, "E79.9.2", {"start": v(-86.99, 0.89) * mm, "mid": v(-90.68, 2.32) * mm, "end": v(-94.12, 4.3) * mm});
            skArc(sketch, "E79.10.0", {"start": v(-83.61, -24) * mm, "mid": v(-86.8, -26.36) * mm, "end": v(-89.58, -29.18) * mm});
            skArc(sketch, "E79.10.1", {"start": v(-83.61, -24) * mm, "mid": v(-81.38, -18.57) * mm, "end": v(-85.75, -14.66) * mm});
            skArc(sketch, "E79.10.2", {"start": v(-85.75, -14.66) * mm, "mid": v(-89.64, -13.9) * mm, "end": v(-93.37, -12.58) * mm});
            skArc(sketch, "E79.11.0", {"start": v(-77.99, -38.54) * mm, "mid": v(-80.7, -41.44) * mm, "end": v(-82.93, -44.7) * mm});
            skArc(sketch, "E79.11.1", {"start": v(-77.99, -38.54) * mm, "mid": v(-76.75, -32.8) * mm, "end": v(-81.75, -29.73) * mm});
            skArc(sketch, "E79.11.2", {"start": v(-81.75, -29.73) * mm, "mid": v(-85.71, -29.69) * mm, "end": v(-89.62, -29.05) * mm});
            skArc(sketch, "E79.12.0", {"start": v(-69.85, -51.85) * mm, "mid": v(-72, -55.18) * mm, "end": v(-73.62, -58.8) * mm});
            skArc(sketch, "E79.12.1", {"start": v(-69.85, -51.85) * mm, "mid": v(-69.66, -45.98) * mm, "end": v(-75.13, -43.85) * mm});
            skArc(sketch, "E79.12.2", {"start": v(-75.13, -43.85) * mm, "mid": v(-79.03, -44.52) * mm, "end": v(-83, -44.59) * mm});
            skArc(sketch, "E79.13.0", {"start": v(-59.47, -63.49) * mm, "mid": v(-60.99, -67.15) * mm, "end": v(-61.94, -71) * mm});
            skArc(sketch, "E79.13.1", {"start": v(-59.47, -63.49) * mm, "mid": v(-60.33, -57.68) * mm, "end": v(-66.1, -56.56) * mm});
            skArc(sketch, "E79.13.2", {"start": v(-66.1, -56.56) * mm, "mid": v(-69.81, -57.91) * mm, "end": v(-73.7, -58.69) * mm});
            skArc(sketch, "E79.14.0", {"start": v(-47.18, -73.09) * mm, "mid": v(-48.02, -76.96) * mm, "end": v(-48.27, -80.91) * mm});
            skArc(sketch, "E79.14.1", {"start": v(-47.18, -73.09) * mm, "mid": v(-49.06, -67.53) * mm, "end": v(-54.93, -67.45) * mm});
            skArc(sketch, "E79.14.2", {"start": v(-54.93, -67.45) * mm, "mid": v(-58.35, -69.45) * mm, "end": v(-62.04, -70.9) * mm});
            skArc(sketch, "E79.15.0", {"start": v(-33.37, -80.33) * mm, "mid": v(-33.5, -84.3) * mm, "end": v(-33.04, -88.23) * mm});
            skArc(sketch, "E79.15.1", {"start": v(-33.37, -80.33) * mm, "mid": v(-36.22, -75.2) * mm, "end": v(-42, -76.18) * mm});
            skArc(sketch, "E79.15.2", {"start": v(-42, -76.18) * mm, "mid": v(-45.01, -78.75) * mm, "end": v(-48.38, -80.84) * mm});
            skArc(sketch, "E79.16.0", {"start": v(-18.5, -85) * mm, "mid": v(-17.92, -88.92) * mm, "end": v(-16.76, -92.71) * mm});
            skArc(sketch, "E79.16.1", {"start": v(-18.5, -85) * mm, "mid": v(-22.2, -80.46) * mm, "end": v(-27.72, -82.45) * mm});
            skArc(sketch, "E79.16.2", {"start": v(-27.72, -82.45) * mm, "mid": v(-30.23, -85.52) * mm, "end": v(-33.17, -88.18) * mm});
            skArc(sketch, "E79.17.0", {"start": v(-3.02, -86.94) * mm, "mid": v(-1.75, -90.7) * mm, "end": v(0.07, -94.21) * mm});
            skArc(sketch, "E79.17.1", {"start": v(-3.02, -86.94) * mm, "mid": v(-7.48, -83.13) * mm, "end": v(-12.56, -86.08) * mm});
            skArc(sketch, "E79.17.2", {"start": v(-12.56, -86.08) * mm, "mid": v(-14.47, -89.55) * mm, "end": v(-16.89, -92.69) * mm});
            skArc(sketch, "E79.18.0", {"start": v(12.56, -86.08) * mm, "mid": v(14.44, -89.5) * mm, "end": v(16.8, -92.6) * mm});
            skArc(sketch, "E79.18.1", {"start": v(12.56, -86.08) * mm, "mid": v(7.48, -83.13) * mm, "end": v(3.02, -86.94) * mm});
            skArc(sketch, "E79.18.2", {"start": v(3.02, -86.94) * mm, "mid": v(1.75, -90.7) * mm, "end": v(-0.07, -94.21) * mm});
            skArc(sketch, "E79.19.0", {"start": v(27.72, -82.45) * mm, "mid": v(30.19, -85.48) * mm, "end": v(33.07, -88.1) * mm});
            skArc(sketch, "E79.19.1", {"start": v(27.72, -82.45) * mm, "mid": v(22.2, -80.46) * mm, "end": v(18.5, -85) * mm});
            skArc(sketch, "E79.19.2", {"start": v(18.5, -85) * mm, "mid": v(17.93, -88.86) * mm, "end": v(16.8, -92.6) * mm});
            skArc(sketch, "E79.20.0", {"start": v(42, -76.18) * mm, "mid": v(44.96, -78.71) * mm, "end": v(48.27, -80.79) * mm});
            skArc(sketch, "E79.20.1", {"start": v(42, -76.18) * mm, "mid": v(36.22, -75.2) * mm, "end": v(33.37, -80.33) * mm});
            skArc(sketch, "E79.20.2", {"start": v(33.37, -80.33) * mm, "mid": v(33.5, -84.23) * mm, "end": v(33.07, -88.1) * mm});
            skArc(sketch, "E79.21.0", {"start": v(54.93, -67.45) * mm, "mid": v(58.3, -69.42) * mm, "end": v(61.92, -70.87) * mm});
            skArc(sketch, "E79.21.1", {"start": v(54.93, -67.45) * mm, "mid": v(49.06, -67.53) * mm, "end": v(47.18, -73.09) * mm});
            skArc(sketch, "E79.21.2", {"start": v(47.18, -73.09) * mm, "mid": v(48, -76.9) * mm, "end": v(48.27, -80.79) * mm});
            skArc(sketch, "E79.22.0", {"start": v(66.1, -56.56) * mm, "mid": v(69.75, -57.9) * mm, "end": v(73.58, -58.67) * mm});
            skArc(sketch, "E79.22.1", {"start": v(66.1, -56.56) * mm, "mid": v(60.33, -57.68) * mm, "end": v(59.47, -63.49) * mm});
            skArc(sketch, "E79.22.2", {"start": v(59.47, -63.49) * mm, "mid": v(60.97, -67.09) * mm, "end": v(61.92, -70.87) * mm});
            skArc(sketch, "E79.23.0", {"start": v(75.13, -43.85) * mm, "mid": v(78.97, -44.51) * mm, "end": v(82.87, -44.6) * mm});
            skArc(sketch, "E79.23.1", {"start": v(75.13, -43.85) * mm, "mid": v(69.66, -45.98) * mm, "end": v(69.85, -51.85) * mm});
            skArc(sketch, "E79.23.2", {"start": v(69.85, -51.85) * mm, "mid": v(71.97, -55.12) * mm, "end": v(73.58, -58.67) * mm});
            skArc(sketch, "E79.24.0", {"start": v(81.75, -29.73) * mm, "mid": v(85.65, -29.7) * mm, "end": v(89.5, -29.08) * mm});
            skArc(sketch, "E79.24.1", {"start": v(81.75, -29.73) * mm, "mid": v(76.75, -32.8) * mm, "end": v(77.99, -38.54) * mm});
            skArc(sketch, "E79.24.2", {"start": v(77.99, -38.54) * mm, "mid": v(80.65, -41.39) * mm, "end": v(82.87, -44.6) * mm});
            skArc(sketch, "E79.25.0", {"start": v(85.75, -14.66) * mm, "mid": v(89.58, -13.92) * mm, "end": v(93.25, -12.63) * mm});
            skArc(sketch, "E79.25.1", {"start": v(85.75, -14.66) * mm, "mid": v(81.38, -18.57) * mm, "end": v(83.61, -24) * mm});
            skArc(sketch, "E79.25.2", {"start": v(83.61, -24) * mm, "mid": v(86.75, -26.32) * mm, "end": v(89.5, -29.08) * mm});
            skArc(sketch, "E79.26.0", {"start": v(86.99, 0.89) * mm, "mid": v(90.62, 2.3) * mm, "end": v(94.01, 4.22) * mm});
            skArc(sketch, "E79.26.1", {"start": v(86.99, 0.89) * mm, "mid": v(83.39, -3.74) * mm, "end": v(86.56, -8.68) * mm});
            skArc(sketch, "E79.26.2", {"start": v(86.56, -8.68) * mm, "mid": v(90.05, -10.4) * mm, "end": v(93.25, -12.63) * mm});
            skArc(sketch, "E79.27.0", {"start": v(85.43, 16.4) * mm, "mid": v(88.76, 18.44) * mm, "end": v(91.75, 20.94) * mm});
            skArc(sketch, "E79.27.1", {"start": v(85.43, 16.4) * mm, "mid": v(82.71, 11.2) * mm, "end": v(86.72, 6.91) * mm});
            skArc(sketch, "E79.27.2", {"start": v(86.72, 6.91) * mm, "mid": v(90.46, 5.84) * mm, "end": v(94.01, 4.22) * mm});
            skArc(sketch, "E79.28.0", {"start": v(81.13, 31.4) * mm, "mid": v(84.04, 34) * mm, "end": v(86.53, 36.99) * mm});
            skArc(sketch, "E79.28.1", {"start": v(81.13, 31.4) * mm, "mid": v(79.38, 25.8) * mm, "end": v(84.09, 22.29) * mm});
            skArc(sketch, "E79.28.2", {"start": v(84.09, 22.29) * mm, "mid": v(87.97, 21.9) * mm, "end": v(91.75, 20.94) * mm});
            skArc(sketch, "E79.29.0", {"start": v(74.22, 45.38) * mm, "mid": v(76.62, 48.45) * mm, "end": v(78.54, 51.84) * mm});
            skArc(sketch, "E79.29.1", {"start": v(74.22, 45.38) * mm, "mid": v(73.5, 39.55) * mm, "end": v(78.76, 36.94) * mm});
            skArc(sketch, "E79.29.2", {"start": v(78.76, 36.94) * mm, "mid": v(82.64, 37.25) * mm, "end": v(86.53, 36.99) * mm});
            skArc(sketch, "E79.30.0", {"start": v(64.92, 57.9) * mm, "mid": v(66.74, 61.35) * mm, "end": v(68.02, 65.03) * mm});
            skArc(sketch, "E79.30.1", {"start": v(64.92, 57.9) * mm, "mid": v(65.26, 52.04) * mm, "end": v(70.9, 50.41) * mm});
            skArc(sketch, "E79.30.2", {"start": v(70.9, 50.41) * mm, "mid": v(74.66, 51.41) * mm, "end": v(78.54, 51.84) * mm});
            skArc(sketch, "E79.31.0", {"start": v(53.54, 68.56) * mm, "mid": v(54.7, 72.28) * mm, "end": v(55.31, 76.13) * mm});
            skArc(sketch, "E79.31.1", {"start": v(53.54, 68.56) * mm, "mid": v(54.92, 62.86) * mm, "end": v(60.75, 62.26) * mm});
            skArc(sketch, "E79.31.2", {"start": v(60.75, 62.26) * mm, "mid": v(64.28, 63.92) * mm, "end": v(68.02, 65.03) * mm});
            skArc(sketch, "E79.32.0", {"start": v(40.44, 77.02) * mm, "mid": v(40.92, 80.89) * mm, "end": v(40.83, 84.79) * mm});
            skArc(sketch, "E79.32.1", {"start": v(40.44, 77.02) * mm, "mid": v(42.81, 71.65) * mm, "end": v(48.66, 72.1) * mm});
            skArc(sketch, "E79.32.2", {"start": v(48.66, 72.1) * mm, "mid": v(51.84, 74.37) * mm, "end": v(55.31, 76.13) * mm});
            skArc(sketch, "E79.33.0", {"start": v(26.04, 83) * mm, "mid": v(25.82, 86.9) * mm, "end": v(25.04, 90.72) * mm});
            skArc(sketch, "E79.33.1", {"start": v(26.04, 83) * mm, "mid": v(29.33, 78.15) * mm, "end": v(35, 79.64) * mm});
            skArc(sketch, "E79.33.2", {"start": v(35, 79.64) * mm, "mid": v(37.73, 82.43) * mm, "end": v(40.83, 84.79) * mm});
            skArc(sketch, "E79.34.0", {"start": v(10.8, 86.32) * mm, "mid": v(9.9, 90.11) * mm, "end": v(8.44, 93.73) * mm});
            skArc(sketch, "E79.34.1", {"start": v(10.8, 86.32) * mm, "mid": v(14.9, 82.13) * mm, "end": v(20.22, 84.6) * mm});
            skArc(sketch, "E79.34.2", {"start": v(20.22, 84.6) * mm, "mid": v(22.4, 87.84) * mm, "end": v(25.04, 90.72) * mm});
            skPoint(sketch, "E80.orphan", {"position": v(-8.38, 93.84) * mm});
            skPoint(sketch, "E81.orphan", {"position": v(8.38, 93.84) * mm});
            skPoint(sketch, "E82.orphan", {"position": v(25, 90.84) * mm});
            skPoint(sketch, "E83.orphan", {"position": v(25.13, 90.8) * mm});
            skPoint(sketch, "E84.orphan", {"position": v(40.82, 84.91) * mm});
            skPoint(sketch, "E85.orphan", {"position": v(40.94, 84.85) * mm});
            skPoint(sketch, "E86.orphan", {"position": v(55.32, 76.26) * mm});
            skPoint(sketch, "E87.orphan", {"position": v(55.43, 76.18) * mm});
            skPoint(sketch, "E88.orphan", {"position": v(68.05, 65.15) * mm});
            skPoint(sketch, "E89.orphan", {"position": v(68.14, 65.06) * mm});
            skPoint(sketch, "E90.orphan", {"position": v(78.6, 51.96) * mm});
            skPoint(sketch, "E91.orphan", {"position": v(78.66, 51.85) * mm});
            skPoint(sketch, "E92.orphan", {"position": v(86.6, 37.09) * mm});
            skPoint(sketch, "E93.orphan", {"position": v(86.66, 36.97) * mm});
            skPoint(sketch, "E94.orphan", {"position": v(91.84, 21.03) * mm});
            skPoint(sketch, "E95.orphan", {"position": v(91.87, 20.9) * mm});
            skPoint(sketch, "E96.orphan", {"position": v(94.12, 4.16) * mm});
            skPoint(sketch, "E97.orphan", {"position": v(94.12, 4.3) * mm});
            skPoint(sketch, "E98.orphan", {"position": v(93.37, -12.58) * mm});
            skPoint(sketch, "E99.orphan", {"position": v(93.35, -12.71) * mm});
            skPoint(sketch, "E100.orphan", {"position": v(89.62, -29.05) * mm});
            skPoint(sketch, "E101.orphan", {"position": v(89.58, -29.18) * mm});
            skPoint(sketch, "E102.orphan", {"position": v(83, -44.59) * mm});
            skPoint(sketch, "E103.orphan", {"position": v(82.93, -44.7) * mm});
            skPoint(sketch, "E104.orphan", {"position": v(73.7, -58.69) * mm});
            skPoint(sketch, "E105.orphan", {"position": v(73.62, -58.8) * mm});
            skPoint(sketch, "E106.orphan", {"position": v(62.04, -70.9) * mm});
            skPoint(sketch, "E107.orphan", {"position": v(61.94, -71) * mm});
            skPoint(sketch, "E108.orphan", {"position": v(48.38, -80.84) * mm});
            skPoint(sketch, "E109.orphan", {"position": v(48.27, -80.91) * mm});
            skPoint(sketch, "E110.orphan", {"position": v(33.17, -88.18) * mm});
            skPoint(sketch, "E111.orphan", {"position": v(33.04, -88.23) * mm});
            skPoint(sketch, "E112.orphan", {"position": v(16.89, -92.69) * mm});
            skPoint(sketch, "E113.orphan", {"position": v(16.76, -92.71) * mm});
            skArc(sketch, "E114.0", {"start": v(-11.51, -59.18) * mm, "mid": v(0.14, -60.16) * mm, "end": v(11.76, -58.85) * mm});
            skArc(sketch, "E115.0", {"start": v(-16.16, -73.03) * mm, "mid": v(-6.75, -65) * mm, "end": v(-5.88, -52.66) * mm});
            skArc(sketch, "E116.0", {"start": v(6.04, -52.22) * mm, "mid": v(6.65, -64.79) * mm, "end": v(16.16, -73.03) * mm});
            skArc(sketch, "E117.0", {"start": v(-14.7, -71.72) * mm, "mid": v(0, -73.23) * mm, "end": v(14.7, -71.72) * mm});
            skSolve(sketch);
        }
        {
            var Q0;
            Q0 = qSketchRegion(id + "F3", true);
            extrude(context, id + "F4", {"entities" : qUnion([Q0]), "depth" : 6 * mm, "offsetDistance" : 25 * mm});
        }
        {
            var Q0;
            Q0=sQuery(id+"F3.wireOp",VERTEX,"E32.1.0");
            var Q1;
            Q1=sQuery(id+"F3.wireOp",VERTEX,"E31");
            var Q2;
            Q2=sQuery(id+"F3.wireOp",VERTEX,"E32.8.0");
            var Q3;
            Q3=sQuery(id+"F3.wireOp",VERTEX,"E32.7.0");
            var Q4;
            Q4=sQuery(id+"F3.wireOp",VERTEX,"E32.6.0");
            var Q5;
            Q5=sQuery(id+"F3.wireOp",VERTEX,"E32.5.0");
            var Q6;
            Q6=sQuery(id+"F3.wireOp",VERTEX,"E32.4.0");
            var Q7;
            Q7=sQuery(id+"F3.wireOp",VERTEX,"E32.3.0");
            var Q8;
            Q8=sQuery(id+"F3.wireOp",VERTEX,"E32.2.0");
            var Q9;
            Q9=makeQuery(id+"F4.opExtrude","SWEPT_BODY",BODY,{"disambiguationData":[OSD([sQuery(id+"F3.wireOp",EDGE,"CO6rlRhf-3iVj-h7l9-1WES-3dDTgxiNE2NJ"),sQuery(id+"F3.wireOp",EDGE,"E33"),sQuery(id+"F3.wireOp",EDGE,"IzWCxFuV-0L88-Bybv-0qDL-taEfpHZzVD9Z"),sQuery(id+"F3.wireOp",EDGE,"S4X2Pr3V-3rsg-3D20-Hteb-AhUWdjDxKGHF"),sQuery(id+"F3.wireOp",EDGE,"E34.1.0"),sQuery(id+"F3.wireOp",EDGE,"E34.1.1"),sQuery(id+"F3.wireOp",EDGE,"E34.1.2"),sQuery(id+"F3.wireOp",EDGE,"E34.2.0"),sQuery(id+"F3.wireOp",EDGE,"E34.2.1"),sQuery(id+"F3.wireOp",EDGE,"E34.2.2"),sQuery(id+"F3.wireOp",EDGE,"E34.3.0"),sQuery(id+"F3.wireOp",EDGE,"E34.3.1"),sQuery(id+"F3.wireOp",EDGE,"E34.3.2"),sQuery(id+"F3.wireOp",EDGE,"E34.4.0"),sQuery(id+"F3.wireOp",EDGE,"E34.4.1"),sQuery(id+"F3.wireOp",EDGE,"E34.4.2"),sQuery(id+"F3.wireOp",EDGE,"E34.5.0"),sQuery(id+"F3.wireOp",EDGE,"E34.5.1"),sQuery(id+"F3.wireOp",EDGE,"E34.5.2"),sQuery(id+"F3.wireOp",EDGE,"E34.6.0"),sQuery(id+"F3.wireOp",EDGE,"E34.6.1"),sQuery(id+"F3.wireOp",EDGE,"E34.6.2"),sQuery(id+"F3.wireOp",EDGE,"E34.7.0"),sQuery(id+"F3.wireOp",EDGE,"E34.7.1"),sQuery(id+"F3.wireOp",EDGE,"E34.7.2"),sQuery(id+"F3.wireOp",EDGE,"E34.8.0"),sQuery(id+"F3.wireOp",EDGE,"E34.8.1"),sQuery(id+"F3.wireOp",EDGE,"E34.8.2"),sQuery(id+"F3.wireOp",EDGE,"E34.9.0"),sQuery(id+"F3.wireOp",EDGE,"E34.9.1"),sQuery(id+"F3.wireOp",EDGE,"E34.9.2"),sQuery(id+"F3.wireOp",EDGE,"E34.10.0"),sQuery(id+"F3.wireOp",EDGE,"E34.10.1"),sQuery(id+"F3.wireOp",EDGE,"E34.10.2"),sQuery(id+"F3.wireOp",EDGE,"E34.11.0"),sQuery(id+"F3.wireOp",EDGE,"E34.11.1"),sQuery(id+"F3.wireOp",EDGE,"E34.11.2"),sQuery(id+"F3.wireOp",EDGE,"E34.12.0"),sQuery(id+"F3.wireOp",EDGE,"E34.12.1"),sQuery(id+"F3.wireOp",EDGE,"E34.12.2"),sQuery(id+"F3.wireOp",EDGE,"E34.13.0"),sQuery(id+"F3.wireOp",EDGE,"E34.13.1"),sQuery(id+"F3.wireOp",EDGE,"E34.13.2"),sQuery(id+"F3.wireOp",EDGE,"E34.14.0"),sQuery(id+"F3.wireOp",EDGE,"E34.14.1"),sQuery(id+"F3.wireOp",EDGE,"E34.14.2"),sQuery(id+"F3.wireOp",EDGE,"E34.15.0"),sQuery(id+"F3.wireOp",EDGE,"E34.15.1"),sQuery(id+"F3.wireOp",EDGE,"E34.15.2"),sQuery(id+"F3.wireOp",EDGE,"E34.16.0"),sQuery(id+"F3.wireOp",EDGE,"E34.16.1"),sQuery(id+"F3.wireOp",EDGE,"E34.16.2"),sQuery(id+"F3.wireOp",EDGE,"E34.17.0"),sQuery(id+"F3.wireOp",EDGE,"E34.17.1"),sQuery(id+"F3.wireOp",EDGE,"E34.17.2"),sQuery(id+"F3.wireOp",EDGE,"E34.18.0"),sQuery(id+"F3.wireOp",EDGE,"E34.18.1"),sQuery(id+"F3.wireOp",EDGE,"E34.18.2"),sQuery(id+"F3.wireOp",EDGE,"E34.19.0"),sQuery(id+"F3.wireOp",EDGE,"E34.19.1"),sQuery(id+"F3.wireOp",EDGE,"E34.19.2"),sQuery(id+"F3.wireOp",EDGE,"E34.20.0"),sQuery(id+"F3.wireOp",EDGE,"E34.20.1"),sQuery(id+"F3.wireOp",EDGE,"E34.20.2"),sQuery(id+"F3.wireOp",EDGE,"E34.21.0"),sQuery(id+"F3.wireOp",EDGE,"E34.21.1"),sQuery(id+"F3.wireOp",EDGE,"E34.21.2"),sQuery(id+"F3.wireOp",EDGE,"E34.22.0"),sQuery(id+"F3.wireOp",EDGE,"E34.22.1"),sQuery(id+"F3.wireOp",EDGE,"E34.22.2"),sQuery(id+"F3.wireOp",EDGE,"E34.23.0"),sQuery(id+"F3.wireOp",EDGE,"E34.23.1"),sQuery(id+"F3.wireOp",EDGE,"E34.23.2"),sQuery(id+"F3.wireOp",EDGE,"E34.24.0"),sQuery(id+"F3.wireOp",EDGE,"E34.24.1"),sQuery(id+"F3.wireOp",EDGE,"E34.24.2"),sQuery(id+"F3.wireOp",EDGE,"E34.25.0"),sQuery(id+"F3.wireOp",EDGE,"E34.25.1"),sQuery(id+"F3.wireOp",EDGE,"E34.25.2"),sQuery(id+"F3.wireOp",EDGE,"E34.26.0"),sQuery(id+"F3.wireOp",EDGE,"E34.26.1"),sQuery(id+"F3.wireOp",EDGE,"E34.26.2"),sQuery(id+"F3.wireOp",EDGE,"E34.27.0"),sQuery(id+"F3.wireOp",EDGE,"E34.27.1"),sQuery(id+"F3.wireOp",EDGE,"E34.27.2"),sQuery(id+"F3.wireOp",EDGE,"E34.28.0"),sQuery(id+"F3.wireOp",EDGE,"E34.28.1"),sQuery(id+"F3.wireOp",EDGE,"E34.28.2"),sQuery(id+"F3.wireOp",EDGE,"E34.29.0"),sQuery(id+"F3.wireOp",EDGE,"E34.29.1"),sQuery(id+"F3.wireOp",EDGE,"E34.29.2"),sQuery(id+"F3.wireOp",EDGE,"E34.30.0"),sQuery(id+"F3.wireOp",EDGE,"E34.30.1"),sQuery(id+"F3.wireOp",EDGE,"E34.30.2"),sQuery(id+"F3.wireOp",EDGE,"E34.31.0"),sQuery(id+"F3.wireOp",EDGE,"E34.31.1"),sQuery(id+"F3.wireOp",EDGE,"E34.31.2"),sQuery(id+"F3.wireOp",EDGE,"E34.32.0"),sQuery(id+"F3.wireOp",EDGE,"E34.32.1"),sQuery(id+"F3.wireOp",EDGE,"E34.32.2"),sQuery(id+"F3.wireOp",EDGE,"E34.33.0"),sQuery(id+"F3.wireOp",EDGE,"E34.33.1"),sQuery(id+"F3.wireOp",EDGE,"E34.33.2"),sQuery(id+"F3.wireOp",EDGE,"E34.34.0"),sQuery(id+"F3.wireOp",EDGE,"E34.34.1"),sQuery(id+"F3.wireOp",EDGE,"E34.34.2")])]});
            hole(context, id + "F5", {"style" : HoleStyle.C_SINK, "endStyle" : HoleEndStyle.THROUGH, "oppositeDirection" : true, "holeDiameter" : 8.2 * mm, "cSinkDiameter" : 16.2 * mm, "cSinkAngle" : 90 * degree, "majorDiameter" : 5 * mm, "isTappedThrough" : true, "tappedDepth" : 12 * mm, "tapClearance" : 3, "startFromSketch" : true, "locations" : qUnion([Q0, Q1, Q2, Q3, Q4, Q5, Q6, Q7, Q8]), "scope" : qUnion([Q9])});
        }
        {
            var Q0;
            Q0=sQuery(id+"F3.wireOp",VERTEX,"E36");
            var Q1;
            Q1=sQuery(id+"F3.wireOp",VERTEX,"E35");
            var Q2;
            Q2=makeQuery(id+"F4.opExtrude","SWEPT_BODY",BODY,{"disambiguationData":[OSD([sQuery(id+"F3.wireOp",EDGE,"CO6rlRhf-3iVj-h7l9-1WES-3dDTgxiNE2NJ"),sQuery(id+"F3.wireOp",EDGE,"E33"),sQuery(id+"F3.wireOp",EDGE,"IzWCxFuV-0L88-Bybv-0qDL-taEfpHZzVD9Z"),sQuery(id+"F3.wireOp",EDGE,"S4X2Pr3V-3rsg-3D20-Hteb-AhUWdjDxKGHF"),sQuery(id+"F3.wireOp",EDGE,"E34.1.0"),sQuery(id+"F3.wireOp",EDGE,"E34.1.1"),sQuery(id+"F3.wireOp",EDGE,"E34.1.2"),sQuery(id+"F3.wireOp",EDGE,"E34.2.0"),sQuery(id+"F3.wireOp",EDGE,"E34.2.1"),sQuery(id+"F3.wireOp",EDGE,"E34.2.2"),sQuery(id+"F3.wireOp",EDGE,"E34.3.0"),sQuery(id+"F3.wireOp",EDGE,"E34.3.1"),sQuery(id+"F3.wireOp",EDGE,"E34.3.2"),sQuery(id+"F3.wireOp",EDGE,"E34.4.0"),sQuery(id+"F3.wireOp",EDGE,"E34.4.1"),sQuery(id+"F3.wireOp",EDGE,"E34.4.2"),sQuery(id+"F3.wireOp",EDGE,"E34.5.0"),sQuery(id+"F3.wireOp",EDGE,"E34.5.1"),sQuery(id+"F3.wireOp",EDGE,"E34.5.2"),sQuery(id+"F3.wireOp",EDGE,"E34.6.0"),sQuery(id+"F3.wireOp",EDGE,"E34.6.1"),sQuery(id+"F3.wireOp",EDGE,"E34.6.2"),sQuery(id+"F3.wireOp",EDGE,"E34.7.0"),sQuery(id+"F3.wireOp",EDGE,"E34.7.1"),sQuery(id+"F3.wireOp",EDGE,"E34.7.2"),sQuery(id+"F3.wireOp",EDGE,"E34.8.0"),sQuery(id+"F3.wireOp",EDGE,"E34.8.1"),sQuery(id+"F3.wireOp",EDGE,"E34.8.2"),sQuery(id+"F3.wireOp",EDGE,"E34.9.0"),sQuery(id+"F3.wireOp",EDGE,"E34.9.1"),sQuery(id+"F3.wireOp",EDGE,"E34.9.2"),sQuery(id+"F3.wireOp",EDGE,"E34.10.0"),sQuery(id+"F3.wireOp",EDGE,"E34.10.1"),sQuery(id+"F3.wireOp",EDGE,"E34.10.2"),sQuery(id+"F3.wireOp",EDGE,"E34.11.0"),sQuery(id+"F3.wireOp",EDGE,"E34.11.1"),sQuery(id+"F3.wireOp",EDGE,"E34.11.2"),sQuery(id+"F3.wireOp",EDGE,"E34.12.0"),sQuery(id+"F3.wireOp",EDGE,"E34.12.1"),sQuery(id+"F3.wireOp",EDGE,"E34.12.2"),sQuery(id+"F3.wireOp",EDGE,"E34.13.0"),sQuery(id+"F3.wireOp",EDGE,"E34.13.1"),sQuery(id+"F3.wireOp",EDGE,"E34.13.2"),sQuery(id+"F3.wireOp",EDGE,"E34.14.0"),sQuery(id+"F3.wireOp",EDGE,"E34.14.1"),sQuery(id+"F3.wireOp",EDGE,"E34.14.2"),sQuery(id+"F3.wireOp",EDGE,"E34.15.0"),sQuery(id+"F3.wireOp",EDGE,"E34.15.1"),sQuery(id+"F3.wireOp",EDGE,"E34.15.2"),sQuery(id+"F3.wireOp",EDGE,"E34.16.0"),sQuery(id+"F3.wireOp",EDGE,"E34.16.1"),sQuery(id+"F3.wireOp",EDGE,"E34.16.2"),sQuery(id+"F3.wireOp",EDGE,"E34.17.0"),sQuery(id+"F3.wireOp",EDGE,"E34.17.1"),sQuery(id+"F3.wireOp",EDGE,"E34.17.2"),sQuery(id+"F3.wireOp",EDGE,"E34.18.0"),sQuery(id+"F3.wireOp",EDGE,"E34.18.1"),sQuery(id+"F3.wireOp",EDGE,"E34.18.2"),sQuery(id+"F3.wireOp",EDGE,"E34.19.0"),sQuery(id+"F3.wireOp",EDGE,"E34.19.1"),sQuery(id+"F3.wireOp",EDGE,"E34.19.2"),sQuery(id+"F3.wireOp",EDGE,"E34.20.0"),sQuery(id+"F3.wireOp",EDGE,"E34.20.1"),sQuery(id+"F3.wireOp",EDGE,"E34.20.2"),sQuery(id+"F3.wireOp",EDGE,"E34.21.0"),sQuery(id+"F3.wireOp",EDGE,"E34.21.1"),sQuery(id+"F3.wireOp",EDGE,"E34.21.2"),sQuery(id+"F3.wireOp",EDGE,"E34.22.0"),sQuery(id+"F3.wireOp",EDGE,"E34.22.1"),sQuery(id+"F3.wireOp",EDGE,"E34.22.2"),sQuery(id+"F3.wireOp",EDGE,"E34.23.0"),sQuery(id+"F3.wireOp",EDGE,"E34.23.1"),sQuery(id+"F3.wireOp",EDGE,"E34.23.2"),sQuery(id+"F3.wireOp",EDGE,"E34.24.0"),sQuery(id+"F3.wireOp",EDGE,"E34.24.1"),sQuery(id+"F3.wireOp",EDGE,"E34.24.2"),sQuery(id+"F3.wireOp",EDGE,"E34.25.0"),sQuery(id+"F3.wireOp",EDGE,"E34.25.1"),sQuery(id+"F3.wireOp",EDGE,"E34.25.2"),sQuery(id+"F3.wireOp",EDGE,"E34.26.0"),sQuery(id+"F3.wireOp",EDGE,"E34.26.1"),sQuery(id+"F3.wireOp",EDGE,"E34.26.2"),sQuery(id+"F3.wireOp",EDGE,"E34.27.0"),sQuery(id+"F3.wireOp",EDGE,"E34.27.1"),sQuery(id+"F3.wireOp",EDGE,"E34.27.2"),sQuery(id+"F3.wireOp",EDGE,"E34.28.0"),sQuery(id+"F3.wireOp",EDGE,"E34.28.1"),sQuery(id+"F3.wireOp",EDGE,"E34.28.2"),sQuery(id+"F3.wireOp",EDGE,"E34.29.0"),sQuery(id+"F3.wireOp",EDGE,"E34.29.1"),sQuery(id+"F3.wireOp",EDGE,"E34.29.2"),sQuery(id+"F3.wireOp",EDGE,"E34.30.0"),sQuery(id+"F3.wireOp",EDGE,"E34.30.1"),sQuery(id+"F3.wireOp",EDGE,"E34.30.2"),sQuery(id+"F3.wireOp",EDGE,"E34.31.0"),sQuery(id+"F3.wireOp",EDGE,"E34.31.1"),sQuery(id+"F3.wireOp",EDGE,"E34.31.2"),sQuery(id+"F3.wireOp",EDGE,"E34.32.0"),sQuery(id+"F3.wireOp",EDGE,"E34.32.1"),sQuery(id+"F3.wireOp",EDGE,"E34.32.2"),sQuery(id+"F3.wireOp",EDGE,"E34.33.0"),sQuery(id+"F3.wireOp",EDGE,"E34.33.1"),sQuery(id+"F3.wireOp",EDGE,"E34.33.2"),sQuery(id+"F3.wireOp",EDGE,"E34.34.0"),sQuery(id+"F3.wireOp",EDGE,"E34.34.1"),sQuery(id+"F3.wireOp",EDGE,"E34.34.2")])]});
            hole(context, id + "F6", {"style" : HoleStyle.C_SINK, "endStyle" : HoleEndStyle.THROUGH, "oppositeDirection" : true, "holeDiameter" : 8.2 * mm, "cSinkDiameter" : 16.2 * mm, "cSinkAngle" : 90 * degree, "majorDiameter" : 5 * mm, "isTappedThrough" : true, "tappedDepth" : 12 * mm, "tapClearance" : 3, "startFromSketch" : true, "locations" : qUnion([Q0, Q1]), "scope" : qUnion([Q2])});
        }
    });
